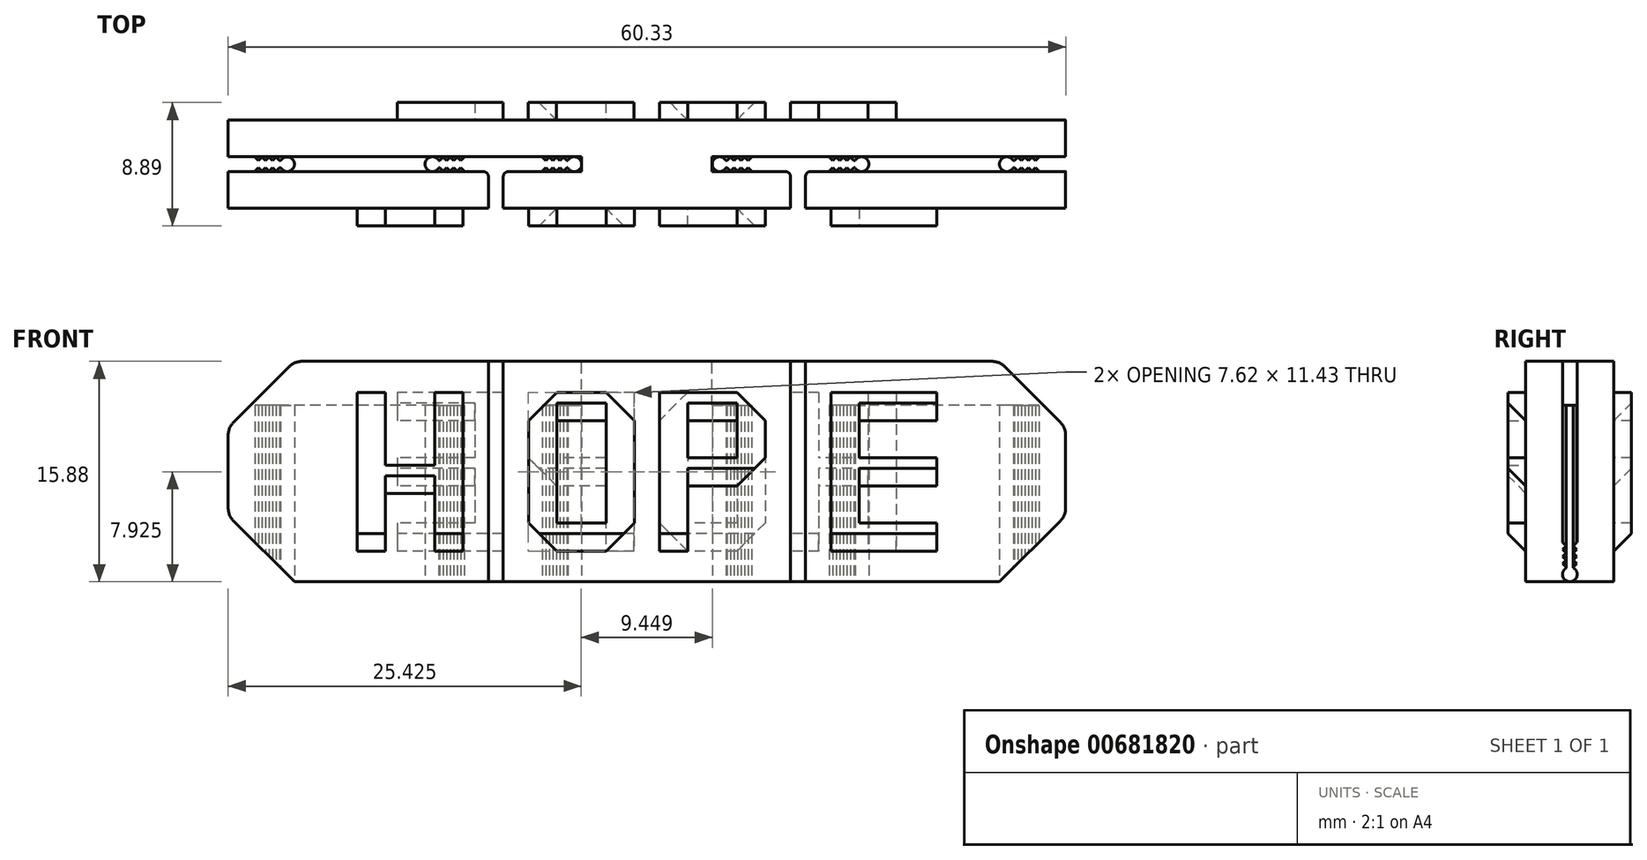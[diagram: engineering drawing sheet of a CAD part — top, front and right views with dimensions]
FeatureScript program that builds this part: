
annotation { "Feature Type Name" : "Feature", "Feature Type Description" : "" }
export const myFeature = defineFeature(function(context is Context, id is Id, definition is map)
    precondition{}
    {
        {
            var Q0;
            Q0=qCreatedBy(makeId("Front.planeOp"),FACE);
            var sketch = newSketch(context, id + "F0", { "sketchPlane" : qUnion([Q0])});
            skLineSegment(sketch, "E0.bottom", {"start": v(0, 0) * mm, "end": v(60.33, 0) * mm});
            skLineSegment(sketch, "E0.top", {"start": v(0, 15.88) * mm, "end": v(60.33, 15.88) * mm});
            skLineSegment(sketch, "E0.left", {"start": v(0, 0) * mm, "end": v(0, 15.88) * mm});
            skLineSegment(sketch, "E0.right", {"start": v(60.33, 0) * mm, "end": v(60.33, 15.88) * mm});
            skSolve(sketch);
        }
        {
            var Q0;
            Q0=makeQuery(id+"F0.imprint","IMPRINT",FACE,{"disambiguationData":[TD([[makeQuery(id+"F0.imprint","IMPRINT",EDGE,{"derivedFrom":sQuery(id+"F0.wireOp",EDGE,"E0.bottom")}),1.0]])]});
            extrude(context, id + "F1", {"entities" : qUnion([Q0]), "depth" : 6.35 * mm, "offsetDistance" : 25.4 * mm});
        }
        {
            var Q0;
            Q0=makeQuery(id+"F1.opExtrude","SWEPT_FACE",FACE,{"disambiguationData":[OSD([sQuery(id+"F0.wireOp",EDGE,"E0.top")])]});
            var sketch = newSketch(context, id + "F2", { "sketchPlane" : qUnion([Q0])});
            skLineSegment(sketch, "E1", {"start": v(0, -2.64) * mm, "end": v(60.33, -2.64) * mm});
            skLineSegment(sketch, "E2", {"start": v(0, -3.7) * mm, "end": v(18.75, -3.7) * mm});
            skLineSegment(sketch, "E3", {"start": v(4.78, -2.64) * mm, "end": v(4.78, -3.7) * mm});
            skLineSegment(sketch, "E4", {"start": v(14.17, -2.64) * mm, "end": v(14.17, -3.7) * mm});
            skLineSegment(sketch, "E5", {"start": v(25.46, -2.64) * mm, "end": v(25.46, -3.7) * mm});
            skLineSegment(sketch, "E6", {"start": v(34.86, -2.64) * mm, "end": v(34.86, -3.7) * mm});
            skLineSegment(sketch, "E7", {"start": v(55.55, -3.7) * mm, "end": v(55.55, -2.64) * mm});
            skLineSegment(sketch, "E8", {"start": v(46.15, -3.7) * mm, "end": v(46.15, -2.64) * mm});
            skLineSegment(sketch, "E9", {"start": v(41.58, -3.7) * mm, "end": v(41.58, -6.35) * mm});
            skLineSegment(sketch, "E10", {"start": v(40.51, -6.35) * mm, "end": v(40.51, -3.7) * mm});
            skLineSegment(sketch, "E11", {"start": v(18.75, -6.35) * mm, "end": v(18.75, -3.7) * mm});
            skLineSegment(sketch, "E12", {"start": v(19.81, -6.35) * mm, "end": v(19.81, -3.7) * mm});
            skLineSegment(sketch, "E13.trimOffspring", {"start": v(41.58, -3.7) * mm, "end": v(60.33, -3.7) * mm});
            skLineSegment(sketch, "E14.trimOffspring", {"start": v(19.81, -3.7) * mm, "end": v(40.51, -3.7) * mm});
            skSolve(sketch);
        }
        {
            var Q0;
            {var subQ3=sQuery(id+"F2.wireOp",EDGE,"E7");Q0=makeQuery(id+"F2.imprint","IMPRINT",FACE,{"disambiguationData":[TD([[makeQuery(id+"F2.imprint","IMPRINT",EDGE,{"derivedFrom":subQ3}),-1.0]])]});}
            var Q1;
            {var subQ2=sQuery(id+"F2.wireOp",EDGE,"E6");Q1=makeQuery(id+"F2.imprint","IMPRINT",FACE,{"disambiguationData":[TD([[makeQuery(id+"F2.imprint","IMPRINT",EDGE,{"derivedFrom":subQ2}),1.0]])]});}
            var Q2;
            {var subQ0=sQuery(id+"F2.wireOp",EDGE,"E4");Q2=makeQuery(id+"F2.imprint","IMPRINT",FACE,{"disambiguationData":[TD([[makeQuery(id+"F2.imprint","IMPRINT",EDGE,{"derivedFrom":subQ0}),1.0]])]});}
            var Q3;
            {var subQ3=sQuery(id+"F2.wireOp",EDGE,"E3");Q3=makeQuery(id+"F2.imprint","IMPRINT",FACE,{"disambiguationData":[TD([[makeQuery(id+"F2.imprint","IMPRINT",EDGE,{"derivedFrom":subQ3}),-1.0]])]});}
            extrude(context, id + "F3", {"entities" : qUnion([Q0, Q1, Q2, Q3]), "operationType" : NewBodyOperationType.REMOVE, "oppositeDirection" : true, "depth" : 25.4 * mm, "offsetDistance" : 25.4 * mm});
        }
        {
            var Q0;
            {var subQ0=sQuery(id+"F0.wireOp",EDGE,"E0.left");var subQ1=sQuery(id+"F0.wireOp",EDGE,"E0.top");var subQ2=sQuery(id+"F2.wireOp",EDGE,"E1");var subQ3=makeQuery(id+"F1.opExtrude","SWEPT_EDGE",EDGE,{"disambiguationData":[OSD([subQ1,subQ0])]});Q0=makeQuery(id+"F3.boolean.opBoolean","SPLIT",EDGE,{"disambiguationData":[TD([makeQuery(id+"F3.opExtrude","SWEPT_FACE",FACE,{"disambiguationData":[OSD([subQ2]),TDD([makeQuery(id+"F2.imprint","IMPRINT",EDGE,{"disambiguationData":[TD([[makeQuery(id+"F2.imprint","INTERSECT",VERTEX,{"derivedFrom":[subQ2,sQuery(id+"F2.wireOp",EDGE,"E3")]}),1.0]])],"derivedFrom":subQ2})])]})])],"derivedFrom":subQ3});}
            var Q1;
            {var subQ0=sQuery(id+"F0.wireOp",EDGE,"E0.left");var subQ1=sQuery(id+"F0.wireOp",EDGE,"E0.top");var subQ2=sQuery(id+"F2.wireOp",EDGE,"E2");var subQ3=makeQuery(id+"F1.opExtrude","SWEPT_EDGE",EDGE,{"disambiguationData":[OSD([subQ1,subQ0])]});Q1=makeQuery(id+"F3.boolean.opBoolean","SPLIT",EDGE,{"disambiguationData":[TD([makeQuery(id+"F3.opExtrude","SWEPT_FACE",FACE,{"disambiguationData":[OSD([subQ2]),TDD([makeQuery(id+"F2.imprint","IMPRINT",EDGE,{"disambiguationData":[TD([[makeQuery(id+"F2.imprint","INTERSECT",VERTEX,{"derivedFrom":[subQ2,sQuery(id+"F2.wireOp",EDGE,"E3")]}),1.0]])],"derivedFrom":subQ2})])]})])],"derivedFrom":subQ3});}
            var Q2;
            {var subQ0=sQuery(id+"F0.wireOp",EDGE,"E0.bottom");var subQ1=sQuery(id+"F2.wireOp",EDGE,"E1");var subQ2=sQuery(id+"F0.wireOp",EDGE,"E0.left");Q2=makeQuery(id+"F3.boolean.opBoolean","SPLIT",EDGE,{"disambiguationData":[TD([makeQuery(id+"F3.opExtrude","SWEPT_FACE",FACE,{"disambiguationData":[OSD([subQ1]),TDD([makeQuery(id+"F2.imprint","IMPRINT",EDGE,{"disambiguationData":[TD([[makeQuery(id+"F2.imprint","INTERSECT",VERTEX,{"derivedFrom":[subQ1,sQuery(id+"F2.wireOp",EDGE,"E3")]}),1.0]])],"derivedFrom":subQ1})])]})])],"derivedFrom":makeQuery(id+"F1.opExtrude","SWEPT_EDGE",EDGE,{"disambiguationData":[OSD([subQ0,subQ2])]})});}
            var Q3;
            {var subQ0=sQuery(id+"F0.wireOp",EDGE,"E0.bottom");var subQ1=sQuery(id+"F0.wireOp",EDGE,"E0.left");var subQ3=sQuery(id+"F2.wireOp",EDGE,"E2");Q3=makeQuery(id+"F3.boolean.opBoolean","SPLIT",EDGE,{"disambiguationData":[TD([makeQuery(id+"F3.opExtrude","SWEPT_FACE",FACE,{"disambiguationData":[OSD([subQ3]),TDD([makeQuery(id+"F2.imprint","IMPRINT",EDGE,{"disambiguationData":[TD([[makeQuery(id+"F2.imprint","INTERSECT",VERTEX,{"derivedFrom":[subQ3,sQuery(id+"F2.wireOp",EDGE,"E3")]}),1.0]])],"derivedFrom":subQ3})])]})])],"derivedFrom":makeQuery(id+"F1.opExtrude","SWEPT_EDGE",EDGE,{"disambiguationData":[OSD([subQ0,subQ1])]})});}
            var Q4;
            {var subQ0=sQuery(id+"F0.wireOp",EDGE,"E0.bottom");var subQ1=sQuery(id+"F0.wireOp",EDGE,"E0.right");var subQ3=sQuery(id+"F2.wireOp",EDGE,"E1");Q4=makeQuery(id+"F3.boolean.opBoolean","SPLIT",EDGE,{"disambiguationData":[TD([makeQuery(id+"F3.opExtrude","SWEPT_FACE",FACE,{"disambiguationData":[OSD([subQ3]),TDD([makeQuery(id+"F2.imprint","IMPRINT",EDGE,{"disambiguationData":[TD([[makeQuery(id+"F2.imprint","INTERSECT",VERTEX,{"derivedFrom":[subQ3,sQuery(id+"F2.wireOp",EDGE,"E7")]}),-1.0]])],"derivedFrom":subQ3})])]})])],"derivedFrom":makeQuery(id+"F1.opExtrude","SWEPT_EDGE",EDGE,{"disambiguationData":[OSD([subQ0,subQ1])]})});}
            var Q5;
            {var subQ0=sQuery(id+"F0.wireOp",EDGE,"E0.bottom");var subQ1=sQuery(id+"F0.wireOp",EDGE,"E0.right");var subQ2=sQuery(id+"F2.wireOp",EDGE,"E13.trimOffspring");Q5=makeQuery(id+"F3.boolean.opBoolean","SPLIT",EDGE,{"disambiguationData":[TD([makeQuery(id+"F3.opExtrude","SWEPT_FACE",FACE,{"disambiguationData":[OSD([subQ2]),TDD([makeQuery(id+"F2.imprint","IMPRINT",EDGE,{"disambiguationData":[TD([[makeQuery(id+"F2.imprint","INTERSECT",VERTEX,{"derivedFrom":[sQuery(id+"F2.wireOp",EDGE,"E7"),subQ2]}),-1.0]])],"derivedFrom":subQ2})])]})])],"derivedFrom":makeQuery(id+"F1.opExtrude","SWEPT_EDGE",EDGE,{"disambiguationData":[OSD([subQ0,subQ1])]})});}
            var Q6;
            {var subQ0=sQuery(id+"F0.wireOp",EDGE,"E0.right");var subQ1=sQuery(id+"F0.wireOp",EDGE,"E0.top");var subQ2=sQuery(id+"F2.wireOp",EDGE,"E13.trimOffspring");var subQ3=makeQuery(id+"F1.opExtrude","SWEPT_EDGE",EDGE,{"disambiguationData":[OSD([subQ1,subQ0])]});Q6=makeQuery(id+"F3.boolean.opBoolean","SPLIT",EDGE,{"disambiguationData":[TD([makeQuery(id+"F3.opExtrude","SWEPT_FACE",FACE,{"disambiguationData":[OSD([subQ2]),TDD([makeQuery(id+"F2.imprint","IMPRINT",EDGE,{"disambiguationData":[TD([[makeQuery(id+"F2.imprint","INTERSECT",VERTEX,{"derivedFrom":[sQuery(id+"F2.wireOp",EDGE,"E7"),subQ2]}),-1.0]])],"derivedFrom":subQ2})])]})])],"derivedFrom":subQ3});}
            var Q7;
            {var subQ0=sQuery(id+"F0.wireOp",EDGE,"E0.right");var subQ1=sQuery(id+"F0.wireOp",EDGE,"E0.top");var subQ2=sQuery(id+"F2.wireOp",EDGE,"E1");var subQ3=makeQuery(id+"F1.opExtrude","SWEPT_EDGE",EDGE,{"disambiguationData":[OSD([subQ1,subQ0])]});Q7=makeQuery(id+"F3.boolean.opBoolean","SPLIT",EDGE,{"disambiguationData":[TD([makeQuery(id+"F3.opExtrude","SWEPT_FACE",FACE,{"disambiguationData":[OSD([subQ2]),TDD([makeQuery(id+"F2.imprint","IMPRINT",EDGE,{"disambiguationData":[TD([[makeQuery(id+"F2.imprint","INTERSECT",VERTEX,{"derivedFrom":[subQ2,sQuery(id+"F2.wireOp",EDGE,"E7")]}),-1.0]])],"derivedFrom":subQ2})])]})])],"derivedFrom":subQ3});}
            chamfer(context, id + "F4", {"entities" : qUnion([Q0, Q1, Q2, Q3, Q4, Q5, Q6, Q7]), "width" : 4.78 * mm, "tangentPropagation" : true});
        }
        {
            var Q0;
            {var subQ0=sQuery(id+"F0.wireOp",EDGE,"E0.bottom");var subQ1=sQuery(id+"F0.wireOp",EDGE,"E0.top");Q0=makeQuery(id+"F3.boolean.opBoolean","SPLIT",FACE,{"disambiguationData":[TD([makeQuery(id+"F3.opExtrude","SWEPT_FACE",FACE,{"disambiguationData":[OSD([sQuery(id+"F2.wireOp",EDGE,"E10")])]})])],"derivedFrom":makeQuery(id+"F1.opExtrude","CAP_FACE",FACE,{"disambiguationData":[OSD([subQ0,subQ1,sQuery(id+"F0.wireOp",EDGE,"E0.left"),sQuery(id+"F0.wireOp",EDGE,"E0.right")])],"isStart":false})});}
            var sketch = newSketch(context, id + "F5", { "sketchPlane" : qUnion([Q0])});
            skLineSegment(sketch, "E15.bottom", {"start": v(23.67, 13.64) * mm, "end": v(27.23, 13.64) * mm});
            skLineSegment(sketch, "E15.top", {"start": v(23.67, 2.2) * mm, "end": v(25.2, 2.2) * mm});
            skLineSegment(sketch, "E15.left", {"start": v(21.64, 11.6) * mm, "end": v(21.64, 6.27) * mm});
            skLineSegment(sketch, "E15.right", {"start": v(29.26, 11.6) * mm, "end": v(29.26, 4.24) * mm});
            skLineSegment(sketch, "E16", {"start": v(21.64, 11.6) * mm, "end": v(23.67, 13.64) * mm});
            skLineSegment(sketch, "E17", {"start": v(27.23, 13.64) * mm, "end": v(29.26, 11.6) * mm});
            skLineSegment(sketch, "E18", {"start": v(21.64, 4.24) * mm, "end": v(23.67, 2.2) * mm});
            skLineSegment(sketch, "E19", {"start": v(27.23, 2.2) * mm, "end": v(29.26, 4.24) * mm});
            skLineSegment(sketch, "E20", {"start": v(21.64, 9.58) * mm, "end": v(25.7, 13.64) * mm});
            skLineSegment(sketch, "E21", {"start": v(25.2, 13.64) * mm, "end": v(29.26, 9.58) * mm});
            skLineSegment(sketch, "E22", {"start": v(21.64, 6.27) * mm, "end": v(25.7, 2.2) * mm});
            skLineSegment(sketch, "E23", {"start": v(25.2, 2.2) * mm, "end": v(29.26, 6.27) * mm});
            skLineSegment(sketch, "E24", {"start": v(21.64, 11.6) * mm, "end": v(29.26, 11.6) * mm});
            skLineSegment(sketch, "E25", {"start": v(23.67, 13.64) * mm, "end": v(23.67, 2.2) * mm});
            skLineSegment(sketch, "E26", {"start": v(21.64, 4.24) * mm, "end": v(29.26, 4.24) * mm});
            skLineSegment(sketch, "E27", {"start": v(27.23, 13.64) * mm, "end": v(27.23, 2.2) * mm});
            skPoint(sketch, "E28.orphan", {"position": v(21.64, 13.64) * mm});
            skPoint(sketch, "E29.orphan", {"position": v(29.26, 13.64) * mm});
            skPoint(sketch, "E30.orphan", {"position": v(29.26, 2.2) * mm});
            skPoint(sketch, "E31.orphan", {"position": v(21.64, 2.2) * mm});
            skLineSegment(sketch, "E32", {"start": v(21.64, 4.24) * mm, "end": v(21.64, 6.27) * mm});
            skLineSegment(sketch, "E33", {"start": v(25.2, 2.2) * mm, "end": v(27.23, 2.2) * mm});
            skLineSegment(sketch, "E34.bottom", {"start": v(31.06, 13.64) * mm, "end": v(36.65, 13.64) * mm});
            skLineSegment(sketch, "E34.top", {"start": v(31.06, 2.2) * mm, "end": v(33.1, 2.2) * mm});
            skLineSegment(sketch, "E34.left", {"start": v(31.06, 13.64) * mm, "end": v(31.06, 2.2) * mm});
            skLineSegment(sketch, "E34.right", {"start": v(38.68, 11.6) * mm, "end": v(38.68, 8.94) * mm});
            skLineSegment(sketch, "E35", {"start": v(33.1, 13.64) * mm, "end": v(33.1, 2.2) * mm});
            skLineSegment(sketch, "E36", {"start": v(31.06, 11.6) * mm, "end": v(38.68, 11.6) * mm});
            skLineSegment(sketch, "E37", {"start": v(36.65, 13.64) * mm, "end": v(38.68, 11.6) * mm});
            skLineSegment(sketch, "E38", {"start": v(31.06, 6.9) * mm, "end": v(36.65, 6.9) * mm});
            skLineSegment(sketch, "E39", {"start": v(31.06, 8.94) * mm, "end": v(38.68, 8.94) * mm});
            skLineSegment(sketch, "E40", {"start": v(36.65, 13.64) * mm, "end": v(36.65, 6.9) * mm});
            skLineSegment(sketch, "E41", {"start": v(36.65, 6.9) * mm, "end": v(38.68, 8.94) * mm});
            skSolve(sketch);
        }
        {
            var Q0;
            {var subQ0=sQuery(id+"F5.wireOp",EDGE,"E17");Q0=makeQuery(id+"F5.imprint","IMPRINT",FACE,{"disambiguationData":[TD([[makeQuery(id+"F5.imprint","IMPRINT",EDGE,{"derivedFrom":subQ0}),-1.0]])]});}
            var Q1;
            {var subQ1=sQuery(id+"F5.wireOp",EDGE,"E15.bottom");var subQ3=sQuery(id+"F5.wireOp",EDGE,"E20");var subQ4=makeQuery(id+"F5.imprint","INTERSECT",VERTEX,{"derivedFrom":[subQ1,subQ3]});Q1=makeQuery(id+"F5.imprint","IMPRINT",FACE,{"disambiguationData":[TD([[makeQuery(id+"F5.imprint","IMPRINT",EDGE,{"disambiguationData":[TD([[subQ4,1.0]])],"derivedFrom":subQ3}),-1.0]])]});}
            var Q2;
            {var subQ0=sQuery(id+"F5.wireOp",EDGE,"E20");var subQ1=sQuery(id+"F5.wireOp",EDGE,"E15.bottom");var subQ2=makeQuery(id+"F5.imprint","INTERSECT",VERTEX,{"derivedFrom":[subQ1,subQ0]});Q2=makeQuery(id+"F5.imprint","IMPRINT",FACE,{"disambiguationData":[TD([[makeQuery(id+"F5.imprint","IMPRINT",EDGE,{"disambiguationData":[TD([[subQ2,1.0]])],"derivedFrom":subQ1}),-1.0]])]});}
            var Q3;
            {var subQ1=sQuery(id+"F5.wireOp",EDGE,"E15.right");var subQ3=sQuery(id+"F5.wireOp",EDGE,"E21");var subQ4=makeQuery(id+"F5.imprint","INTERSECT",VERTEX,{"derivedFrom":[subQ1,subQ3]});Q3=makeQuery(id+"F5.imprint","IMPRINT",FACE,{"disambiguationData":[TD([[makeQuery(id+"F5.imprint","IMPRINT",EDGE,{"disambiguationData":[TD([[subQ4,1.0]])],"derivedFrom":subQ1}),-1.0]])]});}
            var Q4;
            {var subQ0=sQuery(id+"F5.wireOp",EDGE,"E21");var subQ1=sQuery(id+"F5.wireOp",EDGE,"E15.right");var subQ2=makeQuery(id+"F5.imprint","INTERSECT",VERTEX,{"derivedFrom":[subQ1,subQ0]});Q4=makeQuery(id+"F5.imprint","IMPRINT",FACE,{"disambiguationData":[TD([[makeQuery(id+"F5.imprint","IMPRINT",EDGE,{"disambiguationData":[TD([[subQ2,-1.0]])],"derivedFrom":subQ1}),-1.0]])]});}
            var Q5;
            {var subQ1=sQuery(id+"F5.wireOp",EDGE,"E15.right");var subQ3=sQuery(id+"F5.wireOp",EDGE,"E23");var subQ4=makeQuery(id+"F5.imprint","INTERSECT",VERTEX,{"derivedFrom":[subQ1,subQ3]});Q5=makeQuery(id+"F5.imprint","IMPRINT",FACE,{"disambiguationData":[TD([[makeQuery(id+"F5.imprint","IMPRINT",EDGE,{"disambiguationData":[TD([[subQ4,-1.0]])],"derivedFrom":subQ1}),-1.0]])]});}
            var Q6;
            {var subQ0=sQuery(id+"F5.wireOp",EDGE,"E19");Q6=makeQuery(id+"F5.imprint","IMPRINT",FACE,{"disambiguationData":[TD([[makeQuery(id+"F5.imprint","IMPRINT",EDGE,{"derivedFrom":subQ0}),1.0]])]});}
            var Q7;
            {var subQ0=sQuery(id+"F5.wireOp",EDGE,"E33");var subQ1=sQuery(id+"F5.wireOp",EDGE,"E22");var subQ2=makeQuery(id+"F5.imprint","INTERSECT",VERTEX,{"derivedFrom":[subQ1,subQ0]});Q7=makeQuery(id+"F5.imprint","IMPRINT",FACE,{"disambiguationData":[TD([[makeQuery(id+"F5.imprint","IMPRINT",EDGE,{"disambiguationData":[TD([[subQ2,1.0]])],"derivedFrom":subQ1}),1.0]])]});}
            var Q8;
            {var subQ0=sQuery(id+"F5.wireOp",EDGE,"E33");var subQ1=sQuery(id+"F5.wireOp",EDGE,"E22");var subQ2=makeQuery(id+"F5.imprint","INTERSECT",VERTEX,{"derivedFrom":[subQ1,subQ0]});Q8=makeQuery(id+"F5.imprint","IMPRINT",FACE,{"disambiguationData":[TD([[makeQuery(id+"F5.imprint","IMPRINT",EDGE,{"disambiguationData":[TD([[subQ2,1.0]])],"derivedFrom":subQ1}),-1.0]])]});}
            var Q9;
            {var subQ0=sQuery(id+"F5.wireOp",EDGE,"E23");var subQ1=sQuery(id+"F5.wireOp",EDGE,"E22");var subQ2=makeQuery(id+"F5.imprint","INTERSECT",VERTEX,{"derivedFrom":[subQ1,subQ0]});Q9=makeQuery(id+"F5.imprint","IMPRINT",FACE,{"disambiguationData":[TD([[makeQuery(id+"F5.imprint","IMPRINT",EDGE,{"disambiguationData":[TD([[subQ2,1.0]])],"derivedFrom":subQ1}),1.0]])]});}
            var Q10;
            {var subQ0=sQuery(id+"F5.wireOp",EDGE,"E15.top");Q10=makeQuery(id+"F5.imprint","IMPRINT",FACE,{"disambiguationData":[TD([[makeQuery(id+"F5.imprint","IMPRINT",EDGE,{"derivedFrom":subQ0}),1.0]])]});}
            var Q11;
            {var subQ0=sQuery(id+"F5.wireOp",EDGE,"E18");Q11=makeQuery(id+"F5.imprint","IMPRINT",FACE,{"disambiguationData":[TD([[makeQuery(id+"F5.imprint","IMPRINT",EDGE,{"derivedFrom":subQ0}),1.0]])]});}
            var Q12;
            {var subQ0=sQuery(id+"F5.wireOp",EDGE,"E32");Q12=makeQuery(id+"F5.imprint","IMPRINT",FACE,{"disambiguationData":[TD([[makeQuery(id+"F5.imprint","IMPRINT",EDGE,{"derivedFrom":subQ0}),-1.0]])]});}
            var Q13;
            {var subQ1=sQuery(id+"F5.wireOp",EDGE,"E15.left");var subQ3=sQuery(id+"F5.wireOp",EDGE,"E20");var subQ4=makeQuery(id+"F5.imprint","INTERSECT",VERTEX,{"derivedFrom":[subQ1,subQ3]});Q13=makeQuery(id+"F5.imprint","IMPRINT",FACE,{"disambiguationData":[TD([[makeQuery(id+"F5.imprint","IMPRINT",EDGE,{"disambiguationData":[TD([[subQ4,-1.0]])],"derivedFrom":subQ1}),1.0]])]});}
            var Q14;
            {var subQ0=sQuery(id+"F5.wireOp",EDGE,"E21");var subQ1=sQuery(id+"F5.wireOp",EDGE,"E20");var subQ2=makeQuery(id+"F5.imprint","INTERSECT",VERTEX,{"derivedFrom":[subQ1,subQ0]});Q14=makeQuery(id+"F5.imprint","IMPRINT",FACE,{"disambiguationData":[TD([[makeQuery(id+"F5.imprint","IMPRINT",EDGE,{"disambiguationData":[TD([[subQ2,1.0]])],"derivedFrom":subQ1}),-1.0]])]});}
            var Q15;
            {var subQ1=sQuery(id+"F5.wireOp",EDGE,"E15.bottom");var subQ3=sQuery(id+"F5.wireOp",EDGE,"E21");var subQ4=makeQuery(id+"F5.imprint","INTERSECT",VERTEX,{"derivedFrom":[subQ1,subQ3]});Q15=makeQuery(id+"F5.imprint","IMPRINT",FACE,{"disambiguationData":[TD([[makeQuery(id+"F5.imprint","IMPRINT",EDGE,{"disambiguationData":[TD([[subQ4,-1.0]])],"derivedFrom":subQ3}),-1.0]])]});}
            var Q16;
            {var subQ0=sQuery(id+"F5.wireOp",EDGE,"E16");Q16=makeQuery(id+"F5.imprint","IMPRINT",FACE,{"disambiguationData":[TD([[makeQuery(id+"F5.imprint","IMPRINT",EDGE,{"derivedFrom":subQ0}),-1.0]])]});}
            var Q17;
            {var subQ1=sQuery(id+"F5.wireOp",EDGE,"E15.left");var subQ3=sQuery(id+"F5.wireOp",EDGE,"E20");var subQ4=makeQuery(id+"F5.imprint","INTERSECT",VERTEX,{"derivedFrom":[subQ1,subQ3]});Q17=makeQuery(id+"F5.imprint","IMPRINT",FACE,{"disambiguationData":[TD([[makeQuery(id+"F5.imprint","IMPRINT",EDGE,{"disambiguationData":[TD([[subQ4,1.0]])],"derivedFrom":subQ1}),1.0]])]});}
            var Q18;
            {var subQ0=sQuery(id+"F5.wireOp",EDGE,"E34.top");Q18=makeQuery(id+"F5.imprint","IMPRINT",FACE,{"disambiguationData":[TD([[makeQuery(id+"F5.imprint","IMPRINT",EDGE,{"derivedFrom":subQ0}),1.0]])]});}
            var Q19;
            {var subQ0=sQuery(id+"F5.wireOp",EDGE,"E38");var subQ1=sQuery(id+"F5.wireOp",EDGE,"E34.left");var subQ2=makeQuery(id+"F5.imprint","INTERSECT",VERTEX,{"derivedFrom":[subQ1,subQ0]});Q19=makeQuery(id+"F5.imprint","IMPRINT",FACE,{"disambiguationData":[TD([[makeQuery(id+"F5.imprint","IMPRINT",EDGE,{"disambiguationData":[TD([[subQ2,1.0]])],"derivedFrom":subQ1}),1.0]])]});}
            var Q20;
            {var subQ0=sQuery(id+"F5.wireOp",EDGE,"E36");var subQ1=sQuery(id+"F5.wireOp",EDGE,"E34.left");var subQ2=makeQuery(id+"F5.imprint","INTERSECT",VERTEX,{"derivedFrom":[subQ1,subQ0]});Q20=makeQuery(id+"F5.imprint","IMPRINT",FACE,{"disambiguationData":[TD([[makeQuery(id+"F5.imprint","IMPRINT",EDGE,{"disambiguationData":[TD([[subQ2,-1.0]])],"derivedFrom":subQ1}),1.0]])]});}
            var Q21;
            {var subQ0=sQuery(id+"F5.wireOp",EDGE,"E34.left");var subQ1=sQuery(id+"F5.wireOp",EDGE,"E34.bottom");var subQ2=makeQuery(id+"F5.imprint","INTERSECT",VERTEX,{"derivedFrom":[subQ1,subQ0]});Q21=makeQuery(id+"F5.imprint","IMPRINT",FACE,{"disambiguationData":[TD([[makeQuery(id+"F5.imprint","IMPRINT",EDGE,{"disambiguationData":[TD([[subQ2,-1.0]])],"derivedFrom":subQ1}),-1.0]])]});}
            var Q22;
            {var subQ1=sQuery(id+"F5.wireOp",EDGE,"E34.bottom");var subQ3=sQuery(id+"F5.wireOp",EDGE,"E35");var subQ4=makeQuery(id+"F5.imprint","INTERSECT",VERTEX,{"derivedFrom":[subQ1,subQ3]});Q22=makeQuery(id+"F5.imprint","IMPRINT",FACE,{"disambiguationData":[TD([[makeQuery(id+"F5.imprint","IMPRINT",EDGE,{"disambiguationData":[TD([[subQ4,-1.0]])],"derivedFrom":subQ3}),1.0]])]});}
            var Q23;
            {var subQ0=sQuery(id+"F5.wireOp",EDGE,"E39");var subQ1=sQuery(id+"F5.wireOp",EDGE,"E35");var subQ2=makeQuery(id+"F5.imprint","INTERSECT",VERTEX,{"derivedFrom":[subQ1,subQ0]});Q23=makeQuery(id+"F5.imprint","IMPRINT",FACE,{"disambiguationData":[TD([[makeQuery(id+"F5.imprint","IMPRINT",EDGE,{"disambiguationData":[TD([[subQ2,-1.0]])],"derivedFrom":subQ1}),1.0]])]});}
            var Q24;
            {var subQ0=sQuery(id+"F5.wireOp",EDGE,"E41");Q24=makeQuery(id+"F5.imprint","IMPRINT",FACE,{"disambiguationData":[TD([[makeQuery(id+"F5.imprint","IMPRINT",EDGE,{"derivedFrom":subQ0}),1.0]])]});}
            var Q25;
            {var subQ0=sQuery(id+"F5.wireOp",EDGE,"E37");Q25=makeQuery(id+"F5.imprint","IMPRINT",FACE,{"disambiguationData":[TD([[makeQuery(id+"F5.imprint","IMPRINT",EDGE,{"derivedFrom":subQ0}),-1.0]])]});}
            var Q26;
            {var subQ0=sQuery(id+"F5.wireOp",EDGE,"E34.right");Q26=makeQuery(id+"F5.imprint","IMPRINT",FACE,{"disambiguationData":[TD([[makeQuery(id+"F5.imprint","IMPRINT",EDGE,{"derivedFrom":subQ0}),-1.0]])]});}
            extrude(context, id + "F6", {"entities" : qUnion([Q0, Q1, Q2, Q3, Q4, Q5, Q6, Q7, Q8, Q9, Q10, Q11, Q12, Q13, Q14, Q15, Q16, Q17, Q18, Q19, Q20, Q21, Q22, Q23, Q24, Q25, Q26]), "operationType" : NewBodyOperationType.ADD, "depth" : 1.27 * mm, "offsetDistance" : 25.4 * mm});
        }
        {
            var Q0;
            {var subQ0=sQuery(id+"F0.wireOp",EDGE,"E0.bottom");var subQ1=sQuery(id+"F0.wireOp",EDGE,"E0.top");var subQ2=sQuery(id+"F0.wireOp",EDGE,"E0.left");Q0=makeQuery(id+"F3.boolean.opBoolean","SPLIT",FACE,{"disambiguationData":[TD([makeQuery(id+"F1.opExtrude","SWEPT_FACE",FACE,{"disambiguationData":[OSD([subQ2])]})])],"derivedFrom":makeQuery(id+"F1.opExtrude","CAP_FACE",FACE,{"disambiguationData":[OSD([subQ0,subQ1,subQ2,sQuery(id+"F0.wireOp",EDGE,"E0.right")])],"isStart":false})});}
            var sketch = newSketch(context, id + "F7", { "sketchPlane" : qUnion([Q0])});
            skLineSegment(sketch, "E42.bottom", {"start": v(9.3, 13.64) * mm, "end": v(11.33, 13.64) * mm});
            skLineSegment(sketch, "E42.top", {"start": v(9.3, 2.2) * mm, "end": v(11.33, 2.2) * mm});
            skLineSegment(sketch, "E42.left", {"start": v(9.3, 13.64) * mm, "end": v(9.3, 2.2) * mm});
            skLineSegment(sketch, "E42.right", {"start": v(16.92, 13.64) * mm, "end": v(16.92, 2.2) * mm});
            skLineSegment(sketch, "E43", {"start": v(11.33, 13.64) * mm, "end": v(11.33, 2.2) * mm});
            skLineSegment(sketch, "E44", {"start": v(14.88, 13.64) * mm, "end": v(14.88, 2.2) * mm});
            skLineSegment(sketch, "E45", {"start": v(9.3, 8.4) * mm, "end": v(16.92, 8.4) * mm});
            skLineSegment(sketch, "E46", {"start": v(9.3, 6.36) * mm, "end": v(16.92, 6.36) * mm});
            skLineSegment(sketch, "E47.trimOffspring", {"start": v(14.88, 13.64) * mm, "end": v(16.92, 13.64) * mm});
            skLineSegment(sketch, "E48.trimOffspring", {"start": v(14.88, 2.2) * mm, "end": v(16.92, 2.2) * mm});
            skSolve(sketch);
        }
        {
            var Q0;
            {var subQ0=sQuery(id+"F7.wireOp",EDGE,"E47.trimOffspring");Q0=makeQuery(id+"F7.imprint","IMPRINT",FACE,{"disambiguationData":[TD([[makeQuery(id+"F7.imprint","IMPRINT",EDGE,{"derivedFrom":subQ0}),-1.0]])]});}
            var Q1;
            {var subQ0=sQuery(id+"F7.wireOp",EDGE,"E45");var subQ1=sQuery(id+"F7.wireOp",EDGE,"E42.right");var subQ2=makeQuery(id+"F7.imprint","INTERSECT",VERTEX,{"derivedFrom":[subQ1,subQ0]});Q1=makeQuery(id+"F7.imprint","IMPRINT",FACE,{"disambiguationData":[TD([[makeQuery(id+"F7.imprint","IMPRINT",EDGE,{"disambiguationData":[TD([[subQ2,-1.0]])],"derivedFrom":subQ1}),-1.0]])]});}
            var Q2;
            {var subQ0=sQuery(id+"F7.wireOp",EDGE,"E48.trimOffspring");Q2=makeQuery(id+"F7.imprint","IMPRINT",FACE,{"disambiguationData":[TD([[makeQuery(id+"F7.imprint","IMPRINT",EDGE,{"derivedFrom":subQ0}),1.0]])]});}
            var Q3;
            {var subQ0=sQuery(id+"F7.wireOp",EDGE,"E45");var subQ1=sQuery(id+"F7.wireOp",EDGE,"E43");var subQ2=makeQuery(id+"F7.imprint","INTERSECT",VERTEX,{"derivedFrom":[subQ1,subQ0]});Q3=makeQuery(id+"F7.imprint","IMPRINT",FACE,{"disambiguationData":[TD([[makeQuery(id+"F7.imprint","IMPRINT",EDGE,{"disambiguationData":[TD([[subQ2,-1.0]])],"derivedFrom":subQ1}),1.0]])]});}
            var Q4;
            {var subQ0=sQuery(id+"F7.wireOp",EDGE,"E42.bottom");Q4=makeQuery(id+"F7.imprint","IMPRINT",FACE,{"disambiguationData":[TD([[makeQuery(id+"F7.imprint","IMPRINT",EDGE,{"derivedFrom":subQ0}),-1.0]])]});}
            var Q5;
            {var subQ0=sQuery(id+"F7.wireOp",EDGE,"E45");var subQ1=sQuery(id+"F7.wireOp",EDGE,"E42.left");var subQ2=makeQuery(id+"F7.imprint","INTERSECT",VERTEX,{"derivedFrom":[subQ1,subQ0]});Q5=makeQuery(id+"F7.imprint","IMPRINT",FACE,{"disambiguationData":[TD([[makeQuery(id+"F7.imprint","IMPRINT",EDGE,{"disambiguationData":[TD([[subQ2,-1.0]])],"derivedFrom":subQ1}),1.0]])]});}
            var Q6;
            {var subQ0=sQuery(id+"F7.wireOp",EDGE,"E42.top");Q6=makeQuery(id+"F7.imprint","IMPRINT",FACE,{"disambiguationData":[TD([[makeQuery(id+"F7.imprint","IMPRINT",EDGE,{"derivedFrom":subQ0}),1.0]])]});}
            extrude(context, id + "F8", {"entities" : qUnion([Q0, Q1, Q2, Q3, Q4, Q5, Q6]), "operationType" : NewBodyOperationType.ADD, "depth" : 1.27 * mm, "offsetDistance" : 25.4 * mm});
        }
        {
            var Q0;
            {var subQ0=sQuery(id+"F0.wireOp",EDGE,"E0.bottom");var subQ1=sQuery(id+"F0.wireOp",EDGE,"E0.right");var subQ2=sQuery(id+"F0.wireOp",EDGE,"E0.top");Q0=makeQuery(id+"F3.boolean.opBoolean","SPLIT",FACE,{"disambiguationData":[TD([makeQuery(id+"F1.opExtrude","SWEPT_FACE",FACE,{"disambiguationData":[OSD([subQ1])]})])],"derivedFrom":makeQuery(id+"F1.opExtrude","CAP_FACE",FACE,{"disambiguationData":[OSD([subQ0,subQ2,sQuery(id+"F0.wireOp",EDGE,"E0.left"),subQ1])],"isStart":false})});}
            var sketch = newSketch(context, id + "F9", { "sketchPlane" : qUnion([Q0])});
            skLineSegment(sketch, "E49.bottom", {"start": v(43.4, 13.64) * mm, "end": v(51.03, 13.64) * mm});
            skLineSegment(sketch, "E49.top", {"start": v(43.4, 2.2) * mm, "end": v(51.03, 2.2) * mm});
            skLineSegment(sketch, "E49.left", {"start": v(43.4, 13.64) * mm, "end": v(43.4, 2.2) * mm});
            skLineSegment(sketch, "E49.right", {"start": v(51.03, 13.64) * mm, "end": v(51.03, 11.6) * mm});
            skLineSegment(sketch, "E50", {"start": v(45.44, 13.64) * mm, "end": v(45.44, 2.2) * mm});
            skLineSegment(sketch, "E51", {"start": v(43.4, 11.6) * mm, "end": v(51.03, 11.6) * mm});
            skLineSegment(sketch, "E52", {"start": v(43.4, 4.24) * mm, "end": v(51.03, 4.24) * mm});
            skLineSegment(sketch, "E53", {"start": v(43.4, 8.94) * mm, "end": v(51.03, 8.94) * mm});
            skLineSegment(sketch, "E54", {"start": v(43.4, 6.9) * mm, "end": v(51.03, 6.9) * mm});
            skLineSegment(sketch, "E55.trimOffspring", {"start": v(51.03, 8.94) * mm, "end": v(51.03, 6.9) * mm});
            skLineSegment(sketch, "E56.trimOffspring", {"start": v(51.03, 4.24) * mm, "end": v(51.03, 2.2) * mm});
            skSolve(sketch);
        }
        {
            var Q0;
            {var subQ0=sQuery(id+"F9.wireOp",EDGE,"E49.left");var subQ1=sQuery(id+"F9.wireOp",EDGE,"E49.bottom");var subQ2=makeQuery(id+"F9.imprint","INTERSECT",VERTEX,{"derivedFrom":[subQ1,subQ0]});Q0=makeQuery(id+"F9.imprint","IMPRINT",FACE,{"disambiguationData":[TD([[makeQuery(id+"F9.imprint","IMPRINT",EDGE,{"disambiguationData":[TD([[subQ2,-1.0]])],"derivedFrom":subQ1}),-1.0]])]});}
            var Q1;
            {var subQ0=sQuery(id+"F9.wireOp",EDGE,"E49.right");Q1=makeQuery(id+"F9.imprint","IMPRINT",FACE,{"disambiguationData":[TD([[makeQuery(id+"F9.imprint","IMPRINT",EDGE,{"derivedFrom":subQ0}),-1.0]])]});}
            var Q2;
            {var subQ0=sQuery(id+"F9.wireOp",EDGE,"E51");var subQ1=sQuery(id+"F9.wireOp",EDGE,"E49.left");var subQ2=makeQuery(id+"F9.imprint","INTERSECT",VERTEX,{"derivedFrom":[subQ1,subQ0]});Q2=makeQuery(id+"F9.imprint","IMPRINT",FACE,{"disambiguationData":[TD([[makeQuery(id+"F9.imprint","IMPRINT",EDGE,{"disambiguationData":[TD([[subQ2,-1.0]])],"derivedFrom":subQ1}),1.0]])]});}
            var Q3;
            {var subQ0=sQuery(id+"F9.wireOp",EDGE,"E53");var subQ1=sQuery(id+"F9.wireOp",EDGE,"E49.left");var subQ2=makeQuery(id+"F9.imprint","INTERSECT",VERTEX,{"derivedFrom":[subQ1,subQ0]});Q3=makeQuery(id+"F9.imprint","IMPRINT",FACE,{"disambiguationData":[TD([[makeQuery(id+"F9.imprint","IMPRINT",EDGE,{"disambiguationData":[TD([[subQ2,-1.0]])],"derivedFrom":subQ1}),1.0]])]});}
            var Q4;
            {var subQ5=sQuery(id+"F9.wireOp",EDGE,"E55.trimOffspring");Q4=makeQuery(id+"F9.imprint","IMPRINT",FACE,{"disambiguationData":[TD([[makeQuery(id+"F9.imprint","IMPRINT",EDGE,{"derivedFrom":subQ5}),-1.0]])]});}
            var Q5;
            {var subQ0=sQuery(id+"F9.wireOp",EDGE,"E52");var subQ1=sQuery(id+"F9.wireOp",EDGE,"E49.left");var subQ2=makeQuery(id+"F9.imprint","INTERSECT",VERTEX,{"derivedFrom":[subQ1,subQ0]});Q5=makeQuery(id+"F9.imprint","IMPRINT",FACE,{"disambiguationData":[TD([[makeQuery(id+"F9.imprint","IMPRINT",EDGE,{"disambiguationData":[TD([[subQ2,1.0]])],"derivedFrom":subQ1}),1.0]])]});}
            var Q6;
            {var subQ0=sQuery(id+"F9.wireOp",EDGE,"E49.left");var subQ1=sQuery(id+"F9.wireOp",EDGE,"E49.top");var subQ2=makeQuery(id+"F9.imprint","INTERSECT",VERTEX,{"derivedFrom":[subQ1,subQ0]});Q6=makeQuery(id+"F9.imprint","IMPRINT",FACE,{"disambiguationData":[TD([[makeQuery(id+"F9.imprint","IMPRINT",EDGE,{"disambiguationData":[TD([[subQ2,-1.0]])],"derivedFrom":subQ1}),1.0]])]});}
            var Q7;
            {var subQ0=sQuery(id+"F9.wireOp",EDGE,"E56.trimOffspring");Q7=makeQuery(id+"F9.imprint","IMPRINT",FACE,{"disambiguationData":[TD([[makeQuery(id+"F9.imprint","IMPRINT",EDGE,{"derivedFrom":subQ0}),-1.0]])]});}
            extrude(context, id + "F10", {"entities" : qUnion([Q0, Q1, Q2, Q3, Q4, Q5, Q6, Q7]), "operationType" : NewBodyOperationType.ADD, "depth" : 1.27 * mm, "offsetDistance" : 25.4 * mm});
        }
        {
            var Q0;
            Q0=makeQuery(id+"F8.opExtrude","CAP_EDGE",EDGE,{"disambiguationData":[OSD([sQuery(id+"F7.wireOp",EDGE,"E42.top")])],"isStart":false});
            var Q1;
            Q1=makeQuery(id+"F8.opExtrude","CAP_EDGE",EDGE,{"disambiguationData":[OSD([sQuery(id+"F7.wireOp",EDGE,"E48.trimOffspring")])],"isStart":false});
            var Q2;
            Q2=makeQuery(id+"F6.opExtrude","CAP_EDGE",EDGE,{"disambiguationData":[OSD([sQuery(id+"F5.wireOp",EDGE,"E15.top"),sQuery(id+"F5.wireOp",EDGE,"E33")])],"isStart":false});
            var Q3;
            Q3=makeQuery(id+"F6.opExtrude","CAP_EDGE",EDGE,{"disambiguationData":[OSD([sQuery(id+"F5.wireOp",EDGE,"E34.top")])],"isStart":false});
            var Q4;
            Q4=makeQuery(id+"F10.opExtrude","CAP_EDGE",EDGE,{"disambiguationData":[OSD([sQuery(id+"F9.wireOp",EDGE,"E49.top")])],"isStart":false});
            var Q5;
            Q5=makeQuery(id+"F10.opExtrude","CAP_EDGE",EDGE,{"disambiguationData":[OSD([sQuery(id+"F9.wireOp",EDGE,"E54")])],"isStart":false});
            var Q6;
            Q6=makeQuery(id+"F10.opExtrude","CAP_EDGE",EDGE,{"disambiguationData":[OSD([sQuery(id+"F9.wireOp",EDGE,"E51")])],"isStart":false});
            var Q7;
            Q7=makeQuery(id+"F6.opExtrude","CAP_EDGE",EDGE,{"disambiguationData":[OSD([sQuery(id+"F5.wireOp",EDGE,"E36")])],"isStart":false});
            var Q8;
            Q8=makeQuery(id+"F6.opExtrude","CAP_EDGE",EDGE,{"disambiguationData":[OSD([sQuery(id+"F5.wireOp",EDGE,"E24")])],"isStart":false});
            var Q9;
            Q9=makeQuery(id+"F8.opExtrude","CAP_EDGE",EDGE,{"disambiguationData":[OSD([sQuery(id+"F7.wireOp",EDGE,"E46")])],"isStart":false});
            var Q10;
            Q10=makeQuery(id+"F6.opExtrude","CAP_EDGE",EDGE,{"disambiguationData":[OSD([sQuery(id+"F5.wireOp",EDGE,"E38")])],"isStart":false});
            chamfer(context, id + "F11", {"entities" : qUnion([Q0, Q1, Q2, Q3, Q4, Q5, Q6, Q7, Q8, Q9, Q10]), "width" : 1.27 * mm, "tangentPropagation" : true});
        }
        {
            var Q0;
            Q0=makeQuery(id+"F1.opExtrude","CAP_FACE",FACE,{"disambiguationData":[OSD([sQuery(id+"F0.wireOp",EDGE,"E0.bottom"),sQuery(id+"F0.wireOp",EDGE,"E0.top"),sQuery(id+"F0.wireOp",EDGE,"E0.left"),sQuery(id+"F0.wireOp",EDGE,"E0.right")])],"isStart":true});
            var sketch = newSketch(context, id + "F12", { "sketchPlane" : qUnion([Q0])});
            skLineSegment(sketch, "E57.bottom", {"start": v(-36.65, 13.64) * mm, "end": v(-33.1, 13.64) * mm});
            skLineSegment(sketch, "E57.top", {"start": v(-36.65, 2.2) * mm, "end": v(-35.13, 2.2) * mm});
            skLineSegment(sketch, "E57.left", {"start": v(-38.68, 11.6) * mm, "end": v(-38.68, 6.27) * mm});
            skLineSegment(sketch, "E57.right", {"start": v(-31.06, 11.6) * mm, "end": v(-31.06, 4.24) * mm});
            skLineSegment(sketch, "E58", {"start": v(-38.68, 11.6) * mm, "end": v(-36.65, 13.64) * mm});
            skLineSegment(sketch, "E59", {"start": v(-33.1, 13.64) * mm, "end": v(-31.06, 11.6) * mm});
            skLineSegment(sketch, "E60", {"start": v(-38.68, 4.24) * mm, "end": v(-36.65, 2.2) * mm});
            skLineSegment(sketch, "E61", {"start": v(-33.1, 2.2) * mm, "end": v(-31.06, 4.24) * mm});
            skLineSegment(sketch, "E62", {"start": v(-38.68, 9.58) * mm, "end": v(-34.62, 13.64) * mm});
            skLineSegment(sketch, "E63", {"start": v(-35.13, 13.64) * mm, "end": v(-31.06, 9.58) * mm});
            skLineSegment(sketch, "E64", {"start": v(-38.68, 6.27) * mm, "end": v(-34.62, 2.2) * mm});
            skLineSegment(sketch, "E65", {"start": v(-35.13, 2.2) * mm, "end": v(-31.06, 6.27) * mm});
            skLineSegment(sketch, "E66", {"start": v(-38.68, 11.6) * mm, "end": v(-31.06, 11.6) * mm});
            skLineSegment(sketch, "E67", {"start": v(-36.65, 13.64) * mm, "end": v(-36.65, 2.2) * mm});
            skLineSegment(sketch, "E68", {"start": v(-38.68, 4.24) * mm, "end": v(-31.06, 4.24) * mm});
            skLineSegment(sketch, "E69", {"start": v(-33.1, 13.64) * mm, "end": v(-33.1, 2.2) * mm});
            skPoint(sketch, "E70.orphan", {"position": v(-38.68, 13.64) * mm});
            skPoint(sketch, "E71.orphan", {"position": v(-31.06, 13.64) * mm});
            skPoint(sketch, "E72.orphan", {"position": v(-31.06, 2.2) * mm});
            skPoint(sketch, "E73.orphan", {"position": v(-38.68, 2.2) * mm});
            skLineSegment(sketch, "E74", {"start": v(-38.68, 4.24) * mm, "end": v(-38.68, 6.27) * mm});
            skLineSegment(sketch, "E75", {"start": v(-35.13, 2.2) * mm, "end": v(-33.1, 2.2) * mm});
            skLineSegment(sketch, "E76.bottom", {"start": v(-29.24, 13.64) * mm, "end": v(-23.65, 13.64) * mm});
            skLineSegment(sketch, "E76.top", {"start": v(-29.24, 2.2) * mm, "end": v(-27.2, 2.2) * mm});
            skLineSegment(sketch, "E76.left", {"start": v(-29.24, 13.64) * mm, "end": v(-29.24, 2.2) * mm});
            skLineSegment(sketch, "E76.right", {"start": v(-21.62, 11.6) * mm, "end": v(-21.62, 8.94) * mm});
            skLineSegment(sketch, "E77", {"start": v(-27.2, 13.64) * mm, "end": v(-27.2, 2.2) * mm});
            skLineSegment(sketch, "E78", {"start": v(-29.24, 11.6) * mm, "end": v(-21.62, 11.6) * mm});
            skLineSegment(sketch, "E79", {"start": v(-23.65, 13.64) * mm, "end": v(-21.62, 11.6) * mm});
            skLineSegment(sketch, "E80", {"start": v(-29.24, 6.9) * mm, "end": v(-23.65, 6.9) * mm});
            skLineSegment(sketch, "E81", {"start": v(-29.24, 8.94) * mm, "end": v(-21.62, 8.94) * mm});
            skLineSegment(sketch, "E82", {"start": v(-23.65, 13.64) * mm, "end": v(-23.65, 6.9) * mm});
            skLineSegment(sketch, "E83", {"start": v(-23.65, 6.9) * mm, "end": v(-21.62, 8.94) * mm});
            skLineSegment(sketch, "E84.bottom", {"start": v(-48.13, 13.64) * mm, "end": v(-46.1, 13.64) * mm});
            skLineSegment(sketch, "E84.top", {"start": v(-48.13, 2.2) * mm, "end": v(-46.1, 2.2) * mm});
            skLineSegment(sketch, "E84.left", {"start": v(-48.13, 13.64) * mm, "end": v(-48.13, 2.2) * mm});
            skLineSegment(sketch, "E84.right", {"start": v(-40.51, 13.64) * mm, "end": v(-40.51, 2.2) * mm});
            skLineSegment(sketch, "E85", {"start": v(-46.1, 13.64) * mm, "end": v(-46.1, 2.2) * mm});
            skLineSegment(sketch, "E86", {"start": v(-42.55, 13.64) * mm, "end": v(-42.55, 2.2) * mm});
            skLineSegment(sketch, "E87", {"start": v(-48.13, 8.94) * mm, "end": v(-40.51, 8.94) * mm});
            skLineSegment(sketch, "E88", {"start": v(-48.13, 6.9) * mm, "end": v(-40.51, 6.9) * mm});
            skLineSegment(sketch, "E89.trimOffspring", {"start": v(-42.55, 13.64) * mm, "end": v(-40.51, 13.64) * mm});
            skLineSegment(sketch, "E90.trimOffspring", {"start": v(-42.55, 2.2) * mm, "end": v(-40.51, 2.2) * mm});
            skLineSegment(sketch, "E91.bottom", {"start": v(-19.79, 13.64) * mm, "end": v(-12.17, 13.64) * mm});
            skLineSegment(sketch, "E91.top", {"start": v(-19.79, 2.2) * mm, "end": v(-12.17, 2.2) * mm});
            skLineSegment(sketch, "E91.left", {"start": v(-19.79, 13.64) * mm, "end": v(-19.79, 2.2) * mm});
            skLineSegment(sketch, "E91.right", {"start": v(-12.17, 13.64) * mm, "end": v(-12.17, 11.6) * mm});
            skLineSegment(sketch, "E92", {"start": v(-17.75, 13.64) * mm, "end": v(-17.75, 2.2) * mm});
            skLineSegment(sketch, "E93", {"start": v(-19.79, 11.6) * mm, "end": v(-12.17, 11.6) * mm});
            skLineSegment(sketch, "E94", {"start": v(-19.79, 4.24) * mm, "end": v(-12.17, 4.24) * mm});
            skLineSegment(sketch, "E95", {"start": v(-19.79, 8.94) * mm, "end": v(-12.17, 8.94) * mm});
            skLineSegment(sketch, "E96", {"start": v(-19.79, 6.9) * mm, "end": v(-12.17, 6.9) * mm});
            skLineSegment(sketch, "E97.trimOffspring", {"start": v(-12.17, 8.94) * mm, "end": v(-12.17, 6.9) * mm});
            skLineSegment(sketch, "E98.trimOffspring", {"start": v(-12.17, 4.24) * mm, "end": v(-12.17, 2.2) * mm});
            skSolve(sketch);
        }
        {
            var Q0;
            {var subQ0=sQuery(id+"F12.wireOp",EDGE,"E84.bottom");Q0=makeQuery(id+"F12.imprint","IMPRINT",FACE,{"disambiguationData":[TD([[makeQuery(id+"F12.imprint","IMPRINT",EDGE,{"derivedFrom":subQ0}),-1.0]])]});}
            var Q1;
            {var subQ0=sQuery(id+"F12.wireOp",EDGE,"E87");var subQ1=sQuery(id+"F12.wireOp",EDGE,"E84.left");var subQ2=makeQuery(id+"F12.imprint","INTERSECT",VERTEX,{"derivedFrom":[subQ1,subQ0]});Q1=makeQuery(id+"F12.imprint","IMPRINT",FACE,{"disambiguationData":[TD([[makeQuery(id+"F12.imprint","IMPRINT",EDGE,{"disambiguationData":[TD([[subQ2,-1.0]])],"derivedFrom":subQ1}),1.0]])]});}
            var Q2;
            {var subQ0=sQuery(id+"F12.wireOp",EDGE,"E84.top");Q2=makeQuery(id+"F12.imprint","IMPRINT",FACE,{"disambiguationData":[TD([[makeQuery(id+"F12.imprint","IMPRINT",EDGE,{"derivedFrom":subQ0}),1.0]])]});}
            var Q3;
            {var subQ0=sQuery(id+"F12.wireOp",EDGE,"E87");var subQ1=sQuery(id+"F12.wireOp",EDGE,"E85");var subQ2=makeQuery(id+"F12.imprint","INTERSECT",VERTEX,{"derivedFrom":[subQ1,subQ0]});Q3=makeQuery(id+"F12.imprint","IMPRINT",FACE,{"disambiguationData":[TD([[makeQuery(id+"F12.imprint","IMPRINT",EDGE,{"disambiguationData":[TD([[subQ2,-1.0]])],"derivedFrom":subQ1}),1.0]])]});}
            var Q4;
            {var subQ0=sQuery(id+"F12.wireOp",EDGE,"E89.trimOffspring");Q4=makeQuery(id+"F12.imprint","IMPRINT",FACE,{"disambiguationData":[TD([[makeQuery(id+"F12.imprint","IMPRINT",EDGE,{"derivedFrom":subQ0}),-1.0]])]});}
            var Q5;
            {var subQ0=sQuery(id+"F12.wireOp",EDGE,"E90.trimOffspring");Q5=makeQuery(id+"F12.imprint","IMPRINT",FACE,{"disambiguationData":[TD([[makeQuery(id+"F12.imprint","IMPRINT",EDGE,{"derivedFrom":subQ0}),1.0]])]});}
            var Q6;
            {var subQ0=sQuery(id+"F12.wireOp",EDGE,"E87");var subQ1=sQuery(id+"F12.wireOp",EDGE,"E84.right");var subQ2=makeQuery(id+"F12.imprint","INTERSECT",VERTEX,{"derivedFrom":[subQ1,subQ0]});Q6=makeQuery(id+"F12.imprint","IMPRINT",FACE,{"disambiguationData":[TD([[makeQuery(id+"F12.imprint","IMPRINT",EDGE,{"disambiguationData":[TD([[subQ2,-1.0]])],"derivedFrom":subQ1}),-1.0]])]});}
            var Q7;
            {var subQ1=sQuery(id+"F12.wireOp",EDGE,"E57.left");var subQ3=sQuery(id+"F12.wireOp",EDGE,"E62");var subQ4=makeQuery(id+"F12.imprint","INTERSECT",VERTEX,{"derivedFrom":[subQ1,subQ3]});Q7=makeQuery(id+"F12.imprint","IMPRINT",FACE,{"disambiguationData":[TD([[makeQuery(id+"F12.imprint","IMPRINT",EDGE,{"disambiguationData":[TD([[subQ4,1.0]])],"derivedFrom":subQ1}),1.0]])]});}
            var Q8;
            {var subQ0=sQuery(id+"F12.wireOp",EDGE,"E58");Q8=makeQuery(id+"F12.imprint","IMPRINT",FACE,{"disambiguationData":[TD([[makeQuery(id+"F12.imprint","IMPRINT",EDGE,{"derivedFrom":subQ0}),-1.0]])]});}
            var Q9;
            {var subQ1=sQuery(id+"F12.wireOp",EDGE,"E57.bottom");var subQ3=sQuery(id+"F12.wireOp",EDGE,"E63");var subQ4=makeQuery(id+"F12.imprint","INTERSECT",VERTEX,{"derivedFrom":[subQ1,subQ3]});Q9=makeQuery(id+"F12.imprint","IMPRINT",FACE,{"disambiguationData":[TD([[makeQuery(id+"F12.imprint","IMPRINT",EDGE,{"disambiguationData":[TD([[subQ4,-1.0]])],"derivedFrom":subQ3}),-1.0]])]});}
            var Q10;
            {var subQ0=sQuery(id+"F12.wireOp",EDGE,"E62");var subQ1=sQuery(id+"F12.wireOp",EDGE,"E57.bottom");var subQ2=makeQuery(id+"F12.imprint","INTERSECT",VERTEX,{"derivedFrom":[subQ1,subQ0]});Q10=makeQuery(id+"F12.imprint","IMPRINT",FACE,{"disambiguationData":[TD([[makeQuery(id+"F12.imprint","IMPRINT",EDGE,{"disambiguationData":[TD([[subQ2,1.0]])],"derivedFrom":subQ1}),-1.0]])]});}
            var Q11;
            {var subQ0=sQuery(id+"F12.wireOp",EDGE,"E63");var subQ1=sQuery(id+"F12.wireOp",EDGE,"E62");var subQ2=makeQuery(id+"F12.imprint","INTERSECT",VERTEX,{"derivedFrom":[subQ1,subQ0]});Q11=makeQuery(id+"F12.imprint","IMPRINT",FACE,{"disambiguationData":[TD([[makeQuery(id+"F12.imprint","IMPRINT",EDGE,{"disambiguationData":[TD([[subQ2,1.0]])],"derivedFrom":subQ1}),-1.0]])]});}
            var Q12;
            {var subQ1=sQuery(id+"F12.wireOp",EDGE,"E57.bottom");var subQ3=sQuery(id+"F12.wireOp",EDGE,"E62");var subQ4=makeQuery(id+"F12.imprint","INTERSECT",VERTEX,{"derivedFrom":[subQ1,subQ3]});Q12=makeQuery(id+"F12.imprint","IMPRINT",FACE,{"disambiguationData":[TD([[makeQuery(id+"F12.imprint","IMPRINT",EDGE,{"disambiguationData":[TD([[subQ4,1.0]])],"derivedFrom":subQ3}),-1.0]])]});}
            var Q13;
            {var subQ0=sQuery(id+"F12.wireOp",EDGE,"E59");Q13=makeQuery(id+"F12.imprint","IMPRINT",FACE,{"disambiguationData":[TD([[makeQuery(id+"F12.imprint","IMPRINT",EDGE,{"derivedFrom":subQ0}),-1.0]])]});}
            var Q14;
            {var subQ1=sQuery(id+"F12.wireOp",EDGE,"E57.right");var subQ3=sQuery(id+"F12.wireOp",EDGE,"E63");var subQ4=makeQuery(id+"F12.imprint","INTERSECT",VERTEX,{"derivedFrom":[subQ1,subQ3]});Q14=makeQuery(id+"F12.imprint","IMPRINT",FACE,{"disambiguationData":[TD([[makeQuery(id+"F12.imprint","IMPRINT",EDGE,{"disambiguationData":[TD([[subQ4,1.0]])],"derivedFrom":subQ1}),-1.0]])]});}
            var Q15;
            {var subQ1=sQuery(id+"F12.wireOp",EDGE,"E57.left");var subQ3=sQuery(id+"F12.wireOp",EDGE,"E62");var subQ4=makeQuery(id+"F12.imprint","INTERSECT",VERTEX,{"derivedFrom":[subQ1,subQ3]});Q15=makeQuery(id+"F12.imprint","IMPRINT",FACE,{"disambiguationData":[TD([[makeQuery(id+"F12.imprint","IMPRINT",EDGE,{"disambiguationData":[TD([[subQ4,-1.0]])],"derivedFrom":subQ1}),1.0]])]});}
            var Q16;
            {var subQ0=sQuery(id+"F12.wireOp",EDGE,"E74");Q16=makeQuery(id+"F12.imprint","IMPRINT",FACE,{"disambiguationData":[TD([[makeQuery(id+"F12.imprint","IMPRINT",EDGE,{"derivedFrom":subQ0}),-1.0]])]});}
            var Q17;
            {var subQ0=sQuery(id+"F12.wireOp",EDGE,"E60");Q17=makeQuery(id+"F12.imprint","IMPRINT",FACE,{"disambiguationData":[TD([[makeQuery(id+"F12.imprint","IMPRINT",EDGE,{"derivedFrom":subQ0}),1.0]])]});}
            var Q18;
            {var subQ0=sQuery(id+"F12.wireOp",EDGE,"E57.top");Q18=makeQuery(id+"F12.imprint","IMPRINT",FACE,{"disambiguationData":[TD([[makeQuery(id+"F12.imprint","IMPRINT",EDGE,{"derivedFrom":subQ0}),1.0]])]});}
            var Q19;
            {var subQ0=sQuery(id+"F12.wireOp",EDGE,"E75");var subQ1=sQuery(id+"F12.wireOp",EDGE,"E64");var subQ2=makeQuery(id+"F12.imprint","INTERSECT",VERTEX,{"derivedFrom":[subQ1,subQ0]});Q19=makeQuery(id+"F12.imprint","IMPRINT",FACE,{"disambiguationData":[TD([[makeQuery(id+"F12.imprint","IMPRINT",EDGE,{"disambiguationData":[TD([[subQ2,1.0]])],"derivedFrom":subQ1}),-1.0]])]});}
            var Q20;
            {var subQ0=sQuery(id+"F12.wireOp",EDGE,"E65");var subQ1=sQuery(id+"F12.wireOp",EDGE,"E64");var subQ2=makeQuery(id+"F12.imprint","INTERSECT",VERTEX,{"derivedFrom":[subQ1,subQ0]});Q20=makeQuery(id+"F12.imprint","IMPRINT",FACE,{"disambiguationData":[TD([[makeQuery(id+"F12.imprint","IMPRINT",EDGE,{"disambiguationData":[TD([[subQ2,1.0]])],"derivedFrom":subQ1}),1.0]])]});}
            var Q21;
            {var subQ0=sQuery(id+"F12.wireOp",EDGE,"E75");var subQ1=sQuery(id+"F12.wireOp",EDGE,"E64");var subQ2=makeQuery(id+"F12.imprint","INTERSECT",VERTEX,{"derivedFrom":[subQ1,subQ0]});Q21=makeQuery(id+"F12.imprint","IMPRINT",FACE,{"disambiguationData":[TD([[makeQuery(id+"F12.imprint","IMPRINT",EDGE,{"disambiguationData":[TD([[subQ2,1.0]])],"derivedFrom":subQ1}),1.0]])]});}
            var Q22;
            {var subQ0=sQuery(id+"F12.wireOp",EDGE,"E61");Q22=makeQuery(id+"F12.imprint","IMPRINT",FACE,{"disambiguationData":[TD([[makeQuery(id+"F12.imprint","IMPRINT",EDGE,{"derivedFrom":subQ0}),1.0]])]});}
            var Q23;
            {var subQ0=sQuery(id+"F12.wireOp",EDGE,"E63");var subQ1=sQuery(id+"F12.wireOp",EDGE,"E57.right");var subQ2=makeQuery(id+"F12.imprint","INTERSECT",VERTEX,{"derivedFrom":[subQ1,subQ0]});Q23=makeQuery(id+"F12.imprint","IMPRINT",FACE,{"disambiguationData":[TD([[makeQuery(id+"F12.imprint","IMPRINT",EDGE,{"disambiguationData":[TD([[subQ2,-1.0]])],"derivedFrom":subQ1}),-1.0]])]});}
            var Q24;
            {var subQ1=sQuery(id+"F12.wireOp",EDGE,"E57.right");var subQ3=sQuery(id+"F12.wireOp",EDGE,"E65");var subQ4=makeQuery(id+"F12.imprint","INTERSECT",VERTEX,{"derivedFrom":[subQ1,subQ3]});Q24=makeQuery(id+"F12.imprint","IMPRINT",FACE,{"disambiguationData":[TD([[makeQuery(id+"F12.imprint","IMPRINT",EDGE,{"disambiguationData":[TD([[subQ4,-1.0]])],"derivedFrom":subQ1}),-1.0]])]});}
            var Q25;
            {var subQ0=sQuery(id+"F12.wireOp",EDGE,"E76.left");var subQ1=sQuery(id+"F12.wireOp",EDGE,"E76.bottom");var subQ2=makeQuery(id+"F12.imprint","INTERSECT",VERTEX,{"derivedFrom":[subQ1,subQ0]});Q25=makeQuery(id+"F12.imprint","IMPRINT",FACE,{"disambiguationData":[TD([[makeQuery(id+"F12.imprint","IMPRINT",EDGE,{"disambiguationData":[TD([[subQ2,-1.0]])],"derivedFrom":subQ1}),-1.0]])]});}
            var Q26;
            {var subQ1=sQuery(id+"F12.wireOp",EDGE,"E76.bottom");var subQ3=sQuery(id+"F12.wireOp",EDGE,"E77");var subQ4=makeQuery(id+"F12.imprint","INTERSECT",VERTEX,{"derivedFrom":[subQ1,subQ3]});Q26=makeQuery(id+"F12.imprint","IMPRINT",FACE,{"disambiguationData":[TD([[makeQuery(id+"F12.imprint","IMPRINT",EDGE,{"disambiguationData":[TD([[subQ4,-1.0]])],"derivedFrom":subQ3}),1.0]])]});}
            var Q27;
            {var subQ0=sQuery(id+"F12.wireOp",EDGE,"E79");Q27=makeQuery(id+"F12.imprint","IMPRINT",FACE,{"disambiguationData":[TD([[makeQuery(id+"F12.imprint","IMPRINT",EDGE,{"derivedFrom":subQ0}),-1.0]])]});}
            var Q28;
            {var subQ0=sQuery(id+"F12.wireOp",EDGE,"E78");var subQ1=sQuery(id+"F12.wireOp",EDGE,"E76.left");var subQ2=makeQuery(id+"F12.imprint","INTERSECT",VERTEX,{"derivedFrom":[subQ1,subQ0]});Q28=makeQuery(id+"F12.imprint","IMPRINT",FACE,{"disambiguationData":[TD([[makeQuery(id+"F12.imprint","IMPRINT",EDGE,{"disambiguationData":[TD([[subQ2,-1.0]])],"derivedFrom":subQ1}),1.0]])]});}
            var Q29;
            {var subQ0=sQuery(id+"F12.wireOp",EDGE,"E76.right");Q29=makeQuery(id+"F12.imprint","IMPRINT",FACE,{"disambiguationData":[TD([[makeQuery(id+"F12.imprint","IMPRINT",EDGE,{"derivedFrom":subQ0}),-1.0]])]});}
            var Q30;
            {var subQ0=sQuery(id+"F12.wireOp",EDGE,"E80");var subQ1=sQuery(id+"F12.wireOp",EDGE,"E76.left");var subQ2=makeQuery(id+"F12.imprint","INTERSECT",VERTEX,{"derivedFrom":[subQ1,subQ0]});Q30=makeQuery(id+"F12.imprint","IMPRINT",FACE,{"disambiguationData":[TD([[makeQuery(id+"F12.imprint","IMPRINT",EDGE,{"disambiguationData":[TD([[subQ2,1.0]])],"derivedFrom":subQ1}),1.0]])]});}
            var Q31;
            {var subQ0=sQuery(id+"F12.wireOp",EDGE,"E81");var subQ1=sQuery(id+"F12.wireOp",EDGE,"E77");var subQ2=makeQuery(id+"F12.imprint","INTERSECT",VERTEX,{"derivedFrom":[subQ1,subQ0]});Q31=makeQuery(id+"F12.imprint","IMPRINT",FACE,{"disambiguationData":[TD([[makeQuery(id+"F12.imprint","IMPRINT",EDGE,{"disambiguationData":[TD([[subQ2,-1.0]])],"derivedFrom":subQ1}),1.0]])]});}
            var Q32;
            {var subQ0=sQuery(id+"F12.wireOp",EDGE,"E83");Q32=makeQuery(id+"F12.imprint","IMPRINT",FACE,{"disambiguationData":[TD([[makeQuery(id+"F12.imprint","IMPRINT",EDGE,{"derivedFrom":subQ0}),1.0]])]});}
            var Q33;
            {var subQ0=sQuery(id+"F12.wireOp",EDGE,"E76.top");Q33=makeQuery(id+"F12.imprint","IMPRINT",FACE,{"disambiguationData":[TD([[makeQuery(id+"F12.imprint","IMPRINT",EDGE,{"derivedFrom":subQ0}),1.0]])]});}
            var Q34;
            {var subQ0=sQuery(id+"F12.wireOp",EDGE,"E91.left");var subQ1=sQuery(id+"F12.wireOp",EDGE,"E91.bottom");var subQ2=makeQuery(id+"F12.imprint","INTERSECT",VERTEX,{"derivedFrom":[subQ1,subQ0]});Q34=makeQuery(id+"F12.imprint","IMPRINT",FACE,{"disambiguationData":[TD([[makeQuery(id+"F12.imprint","IMPRINT",EDGE,{"disambiguationData":[TD([[subQ2,-1.0]])],"derivedFrom":subQ1}),-1.0]])]});}
            var Q35;
            {var subQ0=sQuery(id+"F12.wireOp",EDGE,"E91.right");Q35=makeQuery(id+"F12.imprint","IMPRINT",FACE,{"disambiguationData":[TD([[makeQuery(id+"F12.imprint","IMPRINT",EDGE,{"derivedFrom":subQ0}),-1.0]])]});}
            var Q36;
            {var subQ0=sQuery(id+"F12.wireOp",EDGE,"E93");var subQ1=sQuery(id+"F12.wireOp",EDGE,"E91.left");var subQ2=makeQuery(id+"F12.imprint","INTERSECT",VERTEX,{"derivedFrom":[subQ1,subQ0]});Q36=makeQuery(id+"F12.imprint","IMPRINT",FACE,{"disambiguationData":[TD([[makeQuery(id+"F12.imprint","IMPRINT",EDGE,{"disambiguationData":[TD([[subQ2,-1.0]])],"derivedFrom":subQ1}),1.0]])]});}
            var Q37;
            {var subQ0=sQuery(id+"F12.wireOp",EDGE,"E95");var subQ1=sQuery(id+"F12.wireOp",EDGE,"E91.left");var subQ2=makeQuery(id+"F12.imprint","INTERSECT",VERTEX,{"derivedFrom":[subQ1,subQ0]});Q37=makeQuery(id+"F12.imprint","IMPRINT",FACE,{"disambiguationData":[TD([[makeQuery(id+"F12.imprint","IMPRINT",EDGE,{"disambiguationData":[TD([[subQ2,-1.0]])],"derivedFrom":subQ1}),1.0]])]});}
            var Q38;
            {var subQ5=sQuery(id+"F12.wireOp",EDGE,"E97.trimOffspring");Q38=makeQuery(id+"F12.imprint","IMPRINT",FACE,{"disambiguationData":[TD([[makeQuery(id+"F12.imprint","IMPRINT",EDGE,{"derivedFrom":subQ5}),-1.0]])]});}
            var Q39;
            {var subQ0=sQuery(id+"F12.wireOp",EDGE,"E94");var subQ1=sQuery(id+"F12.wireOp",EDGE,"E91.left");var subQ2=makeQuery(id+"F12.imprint","INTERSECT",VERTEX,{"derivedFrom":[subQ1,subQ0]});Q39=makeQuery(id+"F12.imprint","IMPRINT",FACE,{"disambiguationData":[TD([[makeQuery(id+"F12.imprint","IMPRINT",EDGE,{"disambiguationData":[TD([[subQ2,1.0]])],"derivedFrom":subQ1}),1.0]])]});}
            var Q40;
            {var subQ0=sQuery(id+"F12.wireOp",EDGE,"E91.left");var subQ1=sQuery(id+"F12.wireOp",EDGE,"E91.top");var subQ2=makeQuery(id+"F12.imprint","INTERSECT",VERTEX,{"derivedFrom":[subQ1,subQ0]});Q40=makeQuery(id+"F12.imprint","IMPRINT",FACE,{"disambiguationData":[TD([[makeQuery(id+"F12.imprint","IMPRINT",EDGE,{"disambiguationData":[TD([[subQ2,-1.0]])],"derivedFrom":subQ1}),1.0]])]});}
            var Q41;
            {var subQ0=sQuery(id+"F12.wireOp",EDGE,"E98.trimOffspring");Q41=makeQuery(id+"F12.imprint","IMPRINT",FACE,{"disambiguationData":[TD([[makeQuery(id+"F12.imprint","IMPRINT",EDGE,{"derivedFrom":subQ0}),-1.0]])]});}
            extrude(context, id + "F13", {"entities" : qUnion([Q0, Q1, Q2, Q3, Q4, Q5, Q6, Q7, Q8, Q9, Q10, Q11, Q12, Q13, Q14, Q15, Q16, Q17, Q18, Q19, Q20, Q21, Q22, Q23, Q24, Q25, Q26, Q27, Q28, Q29, Q30, Q31, Q32, Q33, Q34, Q35, Q36, Q37, Q38, Q39, Q40, Q41]), "operationType" : NewBodyOperationType.ADD, "depth" : 1.27 * mm, "offsetDistance" : 25.4 * mm});
        }
        {
            var Q0;
            Q0=makeQuery(id+"F13.opExtrude","CAP_EDGE",EDGE,{"disambiguationData":[OSD([sQuery(id+"F12.wireOp",EDGE,"E84.top")])],"isStart":false});
            var Q1;
            Q1=makeQuery(id+"F13.opExtrude","CAP_EDGE",EDGE,{"disambiguationData":[OSD([sQuery(id+"F12.wireOp",EDGE,"E88")])],"isStart":false});
            var Q2;
            Q2=makeQuery(id+"F13.opExtrude","CAP_EDGE",EDGE,{"disambiguationData":[OSD([sQuery(id+"F12.wireOp",EDGE,"E90.trimOffspring")])],"isStart":false});
            var Q3;
            Q3=makeQuery(id+"F13.opExtrude","CAP_EDGE",EDGE,{"disambiguationData":[OSD([sQuery(id+"F12.wireOp",EDGE,"E57.top"),sQuery(id+"F12.wireOp",EDGE,"E75")])],"isStart":false});
            var Q4;
            Q4=makeQuery(id+"F13.opExtrude","CAP_EDGE",EDGE,{"disambiguationData":[OSD([sQuery(id+"F12.wireOp",EDGE,"E76.top")])],"isStart":false});
            var Q5;
            Q5=makeQuery(id+"F13.opExtrude","CAP_EDGE",EDGE,{"disambiguationData":[OSD([sQuery(id+"F12.wireOp",EDGE,"E80")])],"isStart":false});
            var Q6;
            Q6=makeQuery(id+"F13.opExtrude","CAP_EDGE",EDGE,{"disambiguationData":[OSD([sQuery(id+"F12.wireOp",EDGE,"E66")])],"isStart":false});
            var Q7;
            Q7=makeQuery(id+"F13.opExtrude","CAP_EDGE",EDGE,{"disambiguationData":[OSD([sQuery(id+"F12.wireOp",EDGE,"E78")])],"isStart":false});
            var Q8;
            Q8=makeQuery(id+"F13.opExtrude","CAP_EDGE",EDGE,{"disambiguationData":[OSD([sQuery(id+"F12.wireOp",EDGE,"E91.top")])],"isStart":false});
            var Q9;
            Q9=makeQuery(id+"F13.opExtrude","CAP_EDGE",EDGE,{"disambiguationData":[OSD([sQuery(id+"F12.wireOp",EDGE,"E96")])],"isStart":false});
            var Q10;
            Q10=makeQuery(id+"F13.opExtrude","CAP_EDGE",EDGE,{"disambiguationData":[OSD([sQuery(id+"F12.wireOp",EDGE,"E93")])],"isStart":false});
            chamfer(context, id + "F14", {"entities" : qUnion([Q0, Q1, Q2, Q3, Q4, Q5, Q6, Q7, Q8, Q9, Q10]), "width" : 1.27 * mm, "tangentPropagation" : true});
        }
        {
            var Q0;
            Q0=makeQuery(id+"F1.opExtrude","SWEPT_FACE",FACE,{"disambiguationData":[OSD([sQuery(id+"F0.wireOp",EDGE,"E0.top")])]});
            var sketch = newSketch(context, id + "F15", { "sketchPlane" : qUnion([Q0])});
            skLineSegment(sketch, "E99", {"start": v(4.78, -2.64) * mm, "end": v(55.55, -2.64) * mm});
            skLineSegment(sketch, "E100", {"start": v(55.55, -2.64) * mm, "end": v(55.55, -3.7) * mm});
            skLineSegment(sketch, "E101", {"start": v(55.55, -3.7) * mm, "end": v(4.78, -3.7) * mm});
            skLineSegment(sketch, "E102", {"start": v(4.78, -3.7) * mm, "end": v(4.78, -2.64) * mm});
            skSolve(sketch);
        }
        {
            var Q0;
            {var subQ2=sQuery(id+"F15.wireOp",EDGE,"E102");Q0=makeQuery(id+"F15.imprint","IMPRINT",FACE,{"disambiguationData":[TD([[makeQuery(id+"F15.imprint","IMPRINT",EDGE,{"derivedFrom":subQ2}),1.0]])]});}
            var Q1;
            {var subQ1=makeQuery(id+"F3.boolean.opBoolean","COPY",EDGE,{"derivedFrom":makeQuery(id+"F3.opExtrude","CAP_EDGE",EDGE,{"disambiguationData":[OSD([sQuery(id+"F2.wireOp",EDGE,"E5")])],"isStart":true})});Q1=makeQuery(id+"F15.imprint","IMPRINT",FACE,{"disambiguationData":[TD([[makeQuery(id+"F15.imprint","IMPRINT",EDGE,{"derivedFrom":subQ1}),1.0]])]});}
            var Q2;
            {var subQ2=sQuery(id+"F15.wireOp",EDGE,"E100");Q2=makeQuery(id+"F15.imprint","IMPRINT",FACE,{"disambiguationData":[TD([[makeQuery(id+"F15.imprint","IMPRINT",EDGE,{"derivedFrom":subQ2}),1.0]])]});}
            extrude(context, id + "F16", {"entities" : qUnion([Q0, Q1, Q2]), "operationType" : NewBodyOperationType.REMOVE, "oppositeDirection" : true, "depth" : 3.17 * mm, "offsetDistance" : 25.4 * mm});
        }
        {
            var Q0;
            Q0=makeQuery(id+"F1.opExtrude","SWEPT_FACE",FACE,{"disambiguationData":[OSD([sQuery(id+"F0.wireOp",EDGE,"E0.bottom")])]});
            var sketch = newSketch(context, id + "F17", { "sketchPlane" : qUnion([Q0])});
            skLineSegment(sketch, "E103.bottom", {"start": v(55.55, 3.7) * mm, "end": v(56.62, 3.7) * mm});
            skLineSegment(sketch, "E103.top", {"start": v(55.55, 2.64) * mm, "end": v(56.62, 2.64) * mm});
            skLineSegment(sketch, "E103.left", {"start": v(55.55, 3.7) * mm, "end": v(55.55, 2.64) * mm});
            skLineSegment(sketch, "E103.right", {"start": v(56.62, 3.7) * mm, "end": v(56.62, 3.43) * mm});
            skLineSegment(sketch, "E104", {"start": v(56.08, 3.7) * mm, "end": v(56.08, 3.7) * mm});
            skArc(sketch, "E105", {"start": v(56.55, 3.43) * mm, "mid": v(55.55, 3.17) * mm, "end": v(56.55, 2.92) * mm});
            skLineSegment(sketch, "E106", {"start": v(55.55, 3.18) * mm, "end": v(55.55, 3.18) * mm});
            skLineSegment(sketch, "E107.trimOffspring", {"start": v(56.08, 2.64) * mm, "end": v(56.08, 2.64) * mm});
            skLineSegment(sketch, "E108.trimOffspring", {"start": v(56.62, 2.92) * mm, "end": v(56.62, 2.64) * mm});
            skLineSegment(sketch, "E109.trimOffspring", {"start": v(56.55, 2.92) * mm, "end": v(56.62, 2.92) * mm});
            skLineSegment(sketch, "E110.trimOffspring", {"start": v(56.55, 3.43) * mm, "end": v(56.62, 3.43) * mm});
            skLineSegment(sketch, "E111.bottom", {"start": v(46.15, 3.7) * mm, "end": v(45.09, 3.7) * mm});
            skLineSegment(sketch, "E111.top", {"start": v(46.15, 2.64) * mm, "end": v(45.09, 2.64) * mm});
            skLineSegment(sketch, "E111.left", {"start": v(46.15, 3.7) * mm, "end": v(46.15, 2.64) * mm});
            skLineSegment(sketch, "E111.right", {"start": v(45.09, 3.7) * mm, "end": v(45.09, 3.43) * mm});
            skLineSegment(sketch, "E112", {"start": v(45.09, 3.18) * mm, "end": v(45.09, 3.18) * mm});
            skArc(sketch, "E113", {"start": v(45.15, 2.92) * mm, "mid": v(46.15, 3.18) * mm, "end": v(45.15, 3.43) * mm});
            skLineSegment(sketch, "E114", {"start": v(45.09, 3.43) * mm, "end": v(45.15, 3.43) * mm});
            skLineSegment(sketch, "E115", {"start": v(45.09, 2.92) * mm, "end": v(45.15, 2.92) * mm});
            skLineSegment(sketch, "E116.trimOffspring", {"start": v(45.09, 2.92) * mm, "end": v(45.09, 2.64) * mm});
            skLineSegment(sketch, "E117.trimOffspring", {"start": v(46.15, 3.18) * mm, "end": v(46.15, 3.18) * mm});
            skLineSegment(sketch, "E118.bottom", {"start": v(34.86, 3.7) * mm, "end": v(35.93, 3.7) * mm});
            skLineSegment(sketch, "E118.top", {"start": v(34.86, 2.64) * mm, "end": v(35.93, 2.64) * mm});
            skLineSegment(sketch, "E118.left", {"start": v(34.86, 3.7) * mm, "end": v(34.86, 2.64) * mm});
            skLineSegment(sketch, "E118.right", {"start": v(35.93, 3.7) * mm, "end": v(35.93, 3.43) * mm});
            skLineSegment(sketch, "E119", {"start": v(34.86, 3.18) * mm, "end": v(34.86, 3.18) * mm});
            skArc(sketch, "E120", {"start": v(35.86, 3.43) * mm, "mid": v(34.86, 3.18) * mm, "end": v(35.86, 2.92) * mm});
            skLineSegment(sketch, "E121.trimOffspring", {"start": v(35.86, 3.43) * mm, "end": v(35.93, 3.43) * mm});
            skLineSegment(sketch, "E122.trimOffspring", {"start": v(35.93, 3.18) * mm, "end": v(35.93, 3.18) * mm});
            skLineSegment(sketch, "E123.trimOffspring", {"start": v(35.86, 2.92) * mm, "end": v(35.93, 2.92) * mm});
            skLineSegment(sketch, "E124.trimOffspring", {"start": v(35.93, 2.92) * mm, "end": v(35.93, 2.64) * mm});
            skLineSegment(sketch, "E125.bottom", {"start": v(25.46, 3.7) * mm, "end": v(24.4, 3.7) * mm});
            skLineSegment(sketch, "E125.top", {"start": v(25.46, 2.64) * mm, "end": v(24.4, 2.64) * mm});
            skLineSegment(sketch, "E125.left", {"start": v(25.46, 3.7) * mm, "end": v(25.46, 2.64) * mm});
            skLineSegment(sketch, "E125.right", {"start": v(24.4, 3.7) * mm, "end": v(24.4, 3.43) * mm});
            skArc(sketch, "E126", {"start": v(24.46, 2.92) * mm, "mid": v(25.46, 3.18) * mm, "end": v(24.46, 3.43) * mm});
            skLineSegment(sketch, "E127", {"start": v(24.4, 3.43) * mm, "end": v(24.46, 3.43) * mm});
            skLineSegment(sketch, "E128", {"start": v(24.4, 2.92) * mm, "end": v(24.46, 2.92) * mm});
            skLineSegment(sketch, "E129.trimOffspring", {"start": v(24.4, 2.92) * mm, "end": v(24.4, 2.64) * mm});
            skPoint(sketch, "E130.orphan", {"position": v(24.4, 3.18) * mm});
            skPoint(sketch, "E131.end.orphan", {"position": v(25.46, 3.18) * mm});
            skLineSegment(sketch, "E132.bottom", {"start": v(14.17, 3.7) * mm, "end": v(15.24, 3.7) * mm});
            skLineSegment(sketch, "E132.top", {"start": v(14.17, 2.64) * mm, "end": v(15.24, 2.64) * mm});
            skLineSegment(sketch, "E132.left", {"start": v(14.17, 3.7) * mm, "end": v(14.17, 2.64) * mm});
            skLineSegment(sketch, "E132.right", {"start": v(15.24, 3.7) * mm, "end": v(15.24, 3.43) * mm});
            skArc(sketch, "E133", {"start": v(15.18, 3.43) * mm, "mid": v(14.17, 3.18) * mm, "end": v(15.18, 2.92) * mm});
            skLineSegment(sketch, "E134.trimOffspring", {"start": v(15.24, 2.92) * mm, "end": v(15.24, 2.64) * mm});
            skLineSegment(sketch, "E135.trimOffspring", {"start": v(15.18, 3.43) * mm, "end": v(15.24, 3.43) * mm});
            skPoint(sketch, "E136.start.orphan", {"position": v(14.17, 3.18) * mm});
            skPoint(sketch, "E137.orphan", {"position": v(15.24, 3.18) * mm});
            skLineSegment(sketch, "E138.trimOffspring", {"start": v(15.18, 2.92) * mm, "end": v(15.24, 2.92) * mm});
            skLineSegment(sketch, "E139.bottom", {"start": v(4.78, 3.7) * mm, "end": v(3.7, 3.7) * mm});
            skLineSegment(sketch, "E139.top", {"start": v(4.78, 2.64) * mm, "end": v(3.7, 2.64) * mm});
            skLineSegment(sketch, "E139.left", {"start": v(4.78, 3.7) * mm, "end": v(4.78, 2.64) * mm});
            skLineSegment(sketch, "E139.right", {"start": v(3.7, 3.7) * mm, "end": v(3.7, 3.43) * mm});
            skLineSegment(sketch, "E140.trimOffspring", {"start": v(3.7, 2.92) * mm, "end": v(3.7, 2.64) * mm});
            skPoint(sketch, "E141.orphan", {"position": v(3.7, 3.18) * mm});
            skPoint(sketch, "E142.end.orphan", {"position": v(4.78, 3.18) * mm});
            skLineSegment(sketch, "E143", {"start": v(4.77, 3.18) * mm, "end": v(4.78, 3.18) * mm});
            skArc(sketch, "E144", {"start": v(3.78, 2.92) * mm, "mid": v(4.77, 3.18) * mm, "end": v(3.78, 3.43) * mm});
            skLineSegment(sketch, "E145", {"start": v(3.7, 3.43) * mm, "end": v(3.78, 3.43) * mm});
            skLineSegment(sketch, "E146", {"start": v(3.7, 2.92) * mm, "end": v(3.78, 2.92) * mm});
            skSolve(sketch);
        }
        {
            var Q0;
            {var subQ0=sQuery(id+"F17.wireOp",EDGE,"E104");Q0=makeQuery(id+"F17.imprint","IMPRINT",FACE,{"disambiguationData":[TD([[makeQuery(id+"F17.imprint","IMPRINT",EDGE,{"derivedFrom":subQ0}),-1.0]])]});}
            var Q1;
            {var subQ0=sQuery(id+"F17.wireOp",EDGE,"E106");Q1=makeQuery(id+"F17.imprint","IMPRINT",FACE,{"disambiguationData":[TD([[makeQuery(id+"F17.imprint","IMPRINT",EDGE,{"derivedFrom":subQ0}),-1.0]])]});}
            var Q2;
            {var subQ2=sQuery(id+"F17.wireOp",EDGE,"E107.trimOffspring");Q2=makeQuery(id+"F17.imprint","IMPRINT",FACE,{"disambiguationData":[TD([[makeQuery(id+"F17.imprint","IMPRINT",EDGE,{"derivedFrom":subQ2}),1.0]])]});}
            var Q3;
            {var subQ3=sQuery(id+"F17.wireOp",EDGE,"E103.right");Q3=makeQuery(id+"F17.imprint","IMPRINT",FACE,{"disambiguationData":[TD([[makeQuery(id+"F17.imprint","IMPRINT",EDGE,{"derivedFrom":subQ3}),-1.0]])]});}
            var Q4;
            {var subQ4=sQuery(id+"F17.wireOp",EDGE,"E111.top");Q4=makeQuery(id+"F17.imprint","IMPRINT",FACE,{"disambiguationData":[TD([[makeQuery(id+"F17.imprint","IMPRINT",EDGE,{"derivedFrom":subQ4}),1.0]])]});}
            var Q5;
            {var subQ4=sQuery(id+"F17.wireOp",EDGE,"E111.bottom");Q5=makeQuery(id+"F17.imprint","IMPRINT",FACE,{"disambiguationData":[TD([[makeQuery(id+"F17.imprint","IMPRINT",EDGE,{"derivedFrom":subQ4}),-1.0]])]});}
            var Q6;
            {var subQ1=sQuery(id+"F17.wireOp",EDGE,"E118.bottom");Q6=makeQuery(id+"F17.imprint","IMPRINT",FACE,{"disambiguationData":[TD([[makeQuery(id+"F17.imprint","IMPRINT",EDGE,{"derivedFrom":subQ1}),-1.0]])]});}
            var Q7;
            {var subQ4=sQuery(id+"F17.wireOp",EDGE,"E118.top");Q7=makeQuery(id+"F17.imprint","IMPRINT",FACE,{"disambiguationData":[TD([[makeQuery(id+"F17.imprint","IMPRINT",EDGE,{"derivedFrom":subQ4}),1.0]])]});}
            var Q8;
            {var subQ0=sQuery(id+"F17.wireOp",EDGE,"E125.left");var subQ1=sQuery(id+"F17.wireOp",EDGE,"E125.bottom");var subQ2=makeQuery(id+"F17.imprint","INTERSECT",VERTEX,{"derivedFrom":[subQ1,subQ0]});Q8=makeQuery(id+"F17.imprint","IMPRINT",FACE,{"disambiguationData":[TD([[makeQuery(id+"F17.imprint","IMPRINT",EDGE,{"disambiguationData":[TD([[subQ2,1.0]])],"derivedFrom":subQ1}),-1.0]])]});}
            var Q9;
            {var subQ0=sQuery(id+"F17.wireOp",EDGE,"E125.left");var subQ1=sQuery(id+"F17.wireOp",EDGE,"E125.top");var subQ2=makeQuery(id+"F17.imprint","INTERSECT",VERTEX,{"derivedFrom":[subQ1,subQ0]});Q9=makeQuery(id+"F17.imprint","IMPRINT",FACE,{"disambiguationData":[TD([[makeQuery(id+"F17.imprint","IMPRINT",EDGE,{"disambiguationData":[TD([[subQ2,1.0]])],"derivedFrom":subQ1}),1.0]])]});}
            var Q10;
            {var subQ5=sQuery(id+"F17.wireOp",EDGE,"E128");Q10=makeQuery(id+"F17.imprint","IMPRINT",FACE,{"disambiguationData":[TD([[makeQuery(id+"F17.imprint","IMPRINT",EDGE,{"derivedFrom":subQ5}),-1.0]])]});}
            var Q11;
            {var subQ0=sQuery(id+"F17.wireOp",EDGE,"E125.right");Q11=makeQuery(id+"F17.imprint","IMPRINT",FACE,{"disambiguationData":[TD([[makeQuery(id+"F17.imprint","IMPRINT",EDGE,{"derivedFrom":subQ0}),1.0]])]});}
            var Q12;
            {var subQ0=sQuery(id+"F17.wireOp",EDGE,"E132.right");Q12=makeQuery(id+"F17.imprint","IMPRINT",FACE,{"disambiguationData":[TD([[makeQuery(id+"F17.imprint","IMPRINT",EDGE,{"derivedFrom":subQ0}),-1.0]])]});}
            var Q13;
            {var subQ0=sQuery(id+"F17.wireOp",EDGE,"E132.left");var subQ1=sQuery(id+"F17.wireOp",EDGE,"E132.bottom");var subQ2=makeQuery(id+"F17.imprint","INTERSECT",VERTEX,{"derivedFrom":[subQ1,subQ0]});Q13=makeQuery(id+"F17.imprint","IMPRINT",FACE,{"disambiguationData":[TD([[makeQuery(id+"F17.imprint","IMPRINT",EDGE,{"disambiguationData":[TD([[subQ2,-1.0]])],"derivedFrom":subQ1}),-1.0]])]});}
            var Q14;
            {var subQ0=sQuery(id+"F17.wireOp",EDGE,"E132.left");var subQ1=sQuery(id+"F17.wireOp",EDGE,"E132.top");var subQ2=makeQuery(id+"F17.imprint","INTERSECT",VERTEX,{"derivedFrom":[subQ1,subQ0]});Q14=makeQuery(id+"F17.imprint","IMPRINT",FACE,{"disambiguationData":[TD([[makeQuery(id+"F17.imprint","IMPRINT",EDGE,{"disambiguationData":[TD([[subQ2,-1.0]])],"derivedFrom":subQ1}),1.0]])]});}
            var Q15;
            {var subQ0=sQuery(id+"F17.wireOp",EDGE,"E134.trimOffspring");Q15=makeQuery(id+"F17.imprint","IMPRINT",FACE,{"disambiguationData":[TD([[makeQuery(id+"F17.imprint","IMPRINT",EDGE,{"derivedFrom":subQ0}),-1.0]])]});}
            var Q16;
            {var subQ1=sQuery(id+"F17.wireOp",EDGE,"E139.bottom");var subQ8=sQuery(id+"F17.wireOp",EDGE,"vViUwkOb-oigo-wygR-mELl-0DaQxFGob972");var subQ9=makeQuery(id+"F17.imprint","INTERSECT",VERTEX,{"derivedFrom":[subQ1,subQ8]});Q16=makeQuery(id+"F17.imprint","IMPRINT",FACE,{"disambiguationData":[TD([[makeQuery(id+"F17.imprint","IMPRINT",EDGE,{"disambiguationData":[TD([[subQ9,1.0]])],"derivedFrom":subQ8}),-1.0]])]});}
            var Q17;
            {var subQ1=sQuery(id+"F17.wireOp",EDGE,"E139.top");var subQ8=sQuery(id+"F17.wireOp",EDGE,"vViUwkOb-oigo-wygR-mELl-0DaQxFGob972");var subQ9=makeQuery(id+"F17.imprint","INTERSECT",VERTEX,{"derivedFrom":[subQ1,subQ8]});Q17=makeQuery(id+"F17.imprint","IMPRINT",FACE,{"disambiguationData":[TD([[makeQuery(id+"F17.imprint","IMPRINT",EDGE,{"disambiguationData":[TD([[subQ9,-1.0]])],"derivedFrom":subQ8}),-1.0]])]});}
            var Q18;
            {var subQ1=sQuery(id+"F17.wireOp",EDGE,"E139.bottom");var subQ8=sQuery(id+"F17.wireOp",EDGE,"4g7BjY2D-837m-m5MQ-NrB3-Du0UvO8V4jLu");var subQ9=makeQuery(id+"F17.imprint","INTERSECT",VERTEX,{"derivedFrom":[subQ1,subQ8]});Q18=makeQuery(id+"F17.imprint","IMPRINT",FACE,{"disambiguationData":[TD([[makeQuery(id+"F17.imprint","IMPRINT",EDGE,{"disambiguationData":[TD([[subQ9,1.0]])],"derivedFrom":subQ8}),-1.0]])]});}
            var Q19;
            {var subQ1=sQuery(id+"F17.wireOp",EDGE,"E139.top");var subQ8=sQuery(id+"F17.wireOp",EDGE,"4g7BjY2D-837m-m5MQ-NrB3-Du0UvO8V4jLu");var subQ9=makeQuery(id+"F17.imprint","INTERSECT",VERTEX,{"derivedFrom":[subQ1,subQ8]});Q19=makeQuery(id+"F17.imprint","IMPRINT",FACE,{"disambiguationData":[TD([[makeQuery(id+"F17.imprint","IMPRINT",EDGE,{"disambiguationData":[TD([[subQ9,-1.0]])],"derivedFrom":subQ8}),-1.0]])]});}
            var Q20;
            {var subQ0=sQuery(id+"F17.wireOp",EDGE,"E139.right");Q20=makeQuery(id+"F17.imprint","IMPRINT",FACE,{"disambiguationData":[TD([[makeQuery(id+"F17.imprint","IMPRINT",EDGE,{"derivedFrom":subQ0}),1.0]])]});}
            var Q21;
            {var subQ4=sQuery(id+"F17.wireOp",EDGE,"k5wNbRY5-FWuI-R7YJ-O7Hm-kdHTz7NwDN8z");Q21=makeQuery(id+"F17.imprint","IMPRINT",FACE,{"disambiguationData":[TD([[makeQuery(id+"F17.imprint","IMPRINT",EDGE,{"derivedFrom":subQ4}),-1.0]])]});}
            var Q22;
            {var subQ1=sQuery(id+"F17.wireOp",EDGE,"E139.top");Q22=makeQuery(id+"F17.imprint","IMPRINT",FACE,{"disambiguationData":[TD([[makeQuery(id+"F17.imprint","IMPRINT",EDGE,{"derivedFrom":subQ1}),-1.0]])]});}
            extrude(context, id + "F18", {"entities" : qUnion([Q0, Q1, Q2, Q3, Q4, Q5, Q6, Q7, Q8, Q9, Q10, Q11, Q12, Q13, Q14, Q15, Q16, Q17, Q18, Q19, Q20, Q21, Q22]), "operationType" : NewBodyOperationType.ADD, "oppositeDirection" : true, "depth" : 12.7 * mm, "offsetDistance" : 25.4 * mm});
        }
        {
            var Q0;
            {var subQ0=sQuery(id+"F0.wireOp",EDGE,"E0.bottom");var subQ2=sQuery(id+"F0.wireOp",EDGE,"E0.left");var subQ5=sQuery(id+"F2.wireOp",EDGE,"E2");var subQ6=makeQuery(id+"F3.opExtrude","SWEPT_FACE",FACE,{"disambiguationData":[OSD([subQ5]),TDD([makeQuery(id+"F2.imprint","IMPRINT",EDGE,{"disambiguationData":[TD([[makeQuery(id+"F2.imprint","INTERSECT",VERTEX,{"derivedFrom":[subQ5,sQuery(id+"F2.wireOp",EDGE,"E3")]}),1.0]])],"derivedFrom":subQ5})])]});var subQ7=makeQuery(id+"F1.opExtrude","SWEPT_FACE",FACE,{"disambiguationData":[OSD([subQ2])]});Q0=makeQuery(id+"F4.opChamfer","BLEND_EDGE",EDGE,{"blendedFrom":[makeQuery(id+"F3.boolean.opBoolean","SPLIT",EDGE,{"disambiguationData":[TD([subQ6])],"derivedFrom":makeQuery(id+"F1.opExtrude","SWEPT_EDGE",EDGE,{"disambiguationData":[OSD([subQ0,subQ2])]})}),makeQuery(id+"F3.boolean.opBoolean","SPLIT",FACE,{"disambiguationData":[TD([subQ6])],"derivedFrom":subQ7})],"blendedInto":[makeQuery(id+"F3.boolean.opBoolean","SPLIT",FACE,{"disambiguationData":[TD([subQ6])],"derivedFrom":subQ7})]});}
            var Q1;
            {var subQ0=sQuery(id+"F0.wireOp",EDGE,"E0.bottom");var subQ2=sQuery(id+"F2.wireOp",EDGE,"E1");var subQ3=sQuery(id+"F0.wireOp",EDGE,"E0.left");var subQ5=makeQuery(id+"F3.opExtrude","SWEPT_FACE",FACE,{"disambiguationData":[OSD([subQ2]),TDD([makeQuery(id+"F2.imprint","IMPRINT",EDGE,{"disambiguationData":[TD([[makeQuery(id+"F2.imprint","INTERSECT",VERTEX,{"derivedFrom":[subQ2,sQuery(id+"F2.wireOp",EDGE,"E3")]}),1.0]])],"derivedFrom":subQ2})])]});var subQ7=makeQuery(id+"F1.opExtrude","SWEPT_FACE",FACE,{"disambiguationData":[OSD([subQ3])]});Q1=makeQuery(id+"F4.opChamfer","BLEND_EDGE",EDGE,{"blendedFrom":[makeQuery(id+"F3.boolean.opBoolean","SPLIT",EDGE,{"disambiguationData":[TD([subQ5])],"derivedFrom":makeQuery(id+"F1.opExtrude","SWEPT_EDGE",EDGE,{"disambiguationData":[OSD([subQ0,subQ3])]})}),makeQuery(id+"F3.boolean.opBoolean","SPLIT",FACE,{"disambiguationData":[TD([subQ5])],"derivedFrom":subQ7})],"blendedInto":[makeQuery(id+"F3.boolean.opBoolean","SPLIT",FACE,{"disambiguationData":[TD([subQ5])],"derivedFrom":subQ7})]});}
            var Q2;
            {var subQ1=sQuery(id+"F2.wireOp",EDGE,"E1");var subQ2=sQuery(id+"F0.wireOp",EDGE,"E0.left");var subQ3=sQuery(id+"F0.wireOp",EDGE,"E0.top");var subQ4=makeQuery(id+"F1.opExtrude","SWEPT_EDGE",EDGE,{"disambiguationData":[OSD([subQ3,subQ2])]});var subQ5=makeQuery(id+"F3.opExtrude","SWEPT_FACE",FACE,{"disambiguationData":[OSD([subQ1]),TDD([makeQuery(id+"F2.imprint","IMPRINT",EDGE,{"disambiguationData":[TD([[makeQuery(id+"F2.imprint","INTERSECT",VERTEX,{"derivedFrom":[subQ1,sQuery(id+"F2.wireOp",EDGE,"E3")]}),1.0]])],"derivedFrom":subQ1})])]});var subQ8=makeQuery(id+"F1.opExtrude","SWEPT_FACE",FACE,{"disambiguationData":[OSD([subQ2])]});Q2=makeQuery(id+"F4.opChamfer","BLEND_EDGE",EDGE,{"blendedFrom":[makeQuery(id+"F3.boolean.opBoolean","SPLIT",EDGE,{"disambiguationData":[TD([subQ5])],"derivedFrom":subQ4}),makeQuery(id+"F3.boolean.opBoolean","SPLIT",FACE,{"disambiguationData":[TD([subQ5])],"derivedFrom":subQ8})],"blendedInto":[makeQuery(id+"F3.boolean.opBoolean","SPLIT",FACE,{"disambiguationData":[TD([subQ5])],"derivedFrom":subQ8})]});}
            var Q3;
            {var subQ1=sQuery(id+"F0.wireOp",EDGE,"E0.left");var subQ2=sQuery(id+"F0.wireOp",EDGE,"E0.top");var subQ4=sQuery(id+"F2.wireOp",EDGE,"E2");var subQ5=makeQuery(id+"F1.opExtrude","SWEPT_EDGE",EDGE,{"disambiguationData":[OSD([subQ2,subQ1])]});var subQ6=makeQuery(id+"F3.opExtrude","SWEPT_FACE",FACE,{"disambiguationData":[OSD([subQ4]),TDD([makeQuery(id+"F2.imprint","IMPRINT",EDGE,{"disambiguationData":[TD([[makeQuery(id+"F2.imprint","INTERSECT",VERTEX,{"derivedFrom":[subQ4,sQuery(id+"F2.wireOp",EDGE,"E3")]}),1.0]])],"derivedFrom":subQ4})])]});var subQ8=makeQuery(id+"F1.opExtrude","SWEPT_FACE",FACE,{"disambiguationData":[OSD([subQ1])]});Q3=makeQuery(id+"F4.opChamfer","BLEND_EDGE",EDGE,{"blendedFrom":[makeQuery(id+"F3.boolean.opBoolean","SPLIT",EDGE,{"disambiguationData":[TD([subQ6])],"derivedFrom":subQ5}),makeQuery(id+"F3.boolean.opBoolean","SPLIT",FACE,{"disambiguationData":[TD([subQ6])],"derivedFrom":subQ8})],"blendedInto":[makeQuery(id+"F3.boolean.opBoolean","SPLIT",FACE,{"disambiguationData":[TD([subQ6])],"derivedFrom":subQ8})]});}
            var Q4;
            {var subQ1=sQuery(id+"F0.wireOp",EDGE,"E0.right");var subQ2=sQuery(id+"F0.wireOp",EDGE,"E0.top");var subQ5=sQuery(id+"F2.wireOp",EDGE,"E1");var subQ6=makeQuery(id+"F1.opExtrude","SWEPT_EDGE",EDGE,{"disambiguationData":[OSD([subQ2,subQ1])]});var subQ7=makeQuery(id+"F3.opExtrude","SWEPT_FACE",FACE,{"disambiguationData":[OSD([subQ5]),TDD([makeQuery(id+"F2.imprint","IMPRINT",EDGE,{"disambiguationData":[TD([[makeQuery(id+"F2.imprint","INTERSECT",VERTEX,{"derivedFrom":[subQ5,sQuery(id+"F2.wireOp",EDGE,"E7")]}),-1.0]])],"derivedFrom":subQ5})])]});var subQ8=makeQuery(id+"F1.opExtrude","SWEPT_FACE",FACE,{"disambiguationData":[OSD([subQ1])]});Q4=makeQuery(id+"F4.opChamfer","BLEND_EDGE",EDGE,{"blendedFrom":[makeQuery(id+"F3.boolean.opBoolean","SPLIT",EDGE,{"disambiguationData":[TD([subQ7])],"derivedFrom":subQ6}),makeQuery(id+"F3.boolean.opBoolean","SPLIT",FACE,{"disambiguationData":[TD([subQ7])],"derivedFrom":subQ8})],"blendedInto":[makeQuery(id+"F3.boolean.opBoolean","SPLIT",FACE,{"disambiguationData":[TD([subQ7])],"derivedFrom":subQ8})]});}
            var Q5;
            {var subQ0=sQuery(id+"F0.wireOp",EDGE,"E0.bottom");var subQ2=sQuery(id+"F0.wireOp",EDGE,"E0.right");var subQ5=sQuery(id+"F2.wireOp",EDGE,"E1");var subQ6=makeQuery(id+"F3.opExtrude","SWEPT_FACE",FACE,{"disambiguationData":[OSD([subQ5]),TDD([makeQuery(id+"F2.imprint","IMPRINT",EDGE,{"disambiguationData":[TD([[makeQuery(id+"F2.imprint","INTERSECT",VERTEX,{"derivedFrom":[subQ5,sQuery(id+"F2.wireOp",EDGE,"E7")]}),-1.0]])],"derivedFrom":subQ5})])]});var subQ7=makeQuery(id+"F1.opExtrude","SWEPT_FACE",FACE,{"disambiguationData":[OSD([subQ2])]});Q5=makeQuery(id+"F4.opChamfer","BLEND_EDGE",EDGE,{"blendedFrom":[makeQuery(id+"F3.boolean.opBoolean","SPLIT",EDGE,{"disambiguationData":[TD([subQ6])],"derivedFrom":makeQuery(id+"F1.opExtrude","SWEPT_EDGE",EDGE,{"disambiguationData":[OSD([subQ0,subQ2])]})}),makeQuery(id+"F3.boolean.opBoolean","SPLIT",FACE,{"disambiguationData":[TD([subQ6])],"derivedFrom":subQ7})],"blendedInto":[makeQuery(id+"F3.boolean.opBoolean","SPLIT",FACE,{"disambiguationData":[TD([subQ6])],"derivedFrom":subQ7})]});}
            var Q6;
            {var subQ0=sQuery(id+"F0.wireOp",EDGE,"E0.bottom");var subQ2=sQuery(id+"F2.wireOp",EDGE,"E13.trimOffspring");var subQ3=sQuery(id+"F0.wireOp",EDGE,"E0.right");var subQ5=makeQuery(id+"F3.opExtrude","SWEPT_FACE",FACE,{"disambiguationData":[OSD([subQ2]),TDD([makeQuery(id+"F2.imprint","IMPRINT",EDGE,{"disambiguationData":[TD([[makeQuery(id+"F2.imprint","INTERSECT",VERTEX,{"derivedFrom":[sQuery(id+"F2.wireOp",EDGE,"E7"),subQ2]}),-1.0]])],"derivedFrom":subQ2})])]});var subQ7=makeQuery(id+"F1.opExtrude","SWEPT_FACE",FACE,{"disambiguationData":[OSD([subQ3])]});Q6=makeQuery(id+"F4.opChamfer","BLEND_EDGE",EDGE,{"blendedFrom":[makeQuery(id+"F3.boolean.opBoolean","SPLIT",EDGE,{"disambiguationData":[TD([subQ5])],"derivedFrom":makeQuery(id+"F1.opExtrude","SWEPT_EDGE",EDGE,{"disambiguationData":[OSD([subQ0,subQ3])]})}),makeQuery(id+"F3.boolean.opBoolean","SPLIT",FACE,{"disambiguationData":[TD([subQ5])],"derivedFrom":subQ7})],"blendedInto":[makeQuery(id+"F3.boolean.opBoolean","SPLIT",FACE,{"disambiguationData":[TD([subQ5])],"derivedFrom":subQ7})]});}
            var Q7;
            {var subQ1=sQuery(id+"F2.wireOp",EDGE,"E13.trimOffspring");var subQ2=sQuery(id+"F0.wireOp",EDGE,"E0.right");var subQ3=sQuery(id+"F0.wireOp",EDGE,"E0.top");var subQ4=makeQuery(id+"F1.opExtrude","SWEPT_EDGE",EDGE,{"disambiguationData":[OSD([subQ3,subQ2])]});var subQ5=makeQuery(id+"F3.opExtrude","SWEPT_FACE",FACE,{"disambiguationData":[OSD([subQ1]),TDD([makeQuery(id+"F2.imprint","IMPRINT",EDGE,{"disambiguationData":[TD([[makeQuery(id+"F2.imprint","INTERSECT",VERTEX,{"derivedFrom":[sQuery(id+"F2.wireOp",EDGE,"E7"),subQ1]}),-1.0]])],"derivedFrom":subQ1})])]});var subQ8=makeQuery(id+"F1.opExtrude","SWEPT_FACE",FACE,{"disambiguationData":[OSD([subQ2])]});Q7=makeQuery(id+"F4.opChamfer","BLEND_EDGE",EDGE,{"blendedFrom":[makeQuery(id+"F3.boolean.opBoolean","SPLIT",EDGE,{"disambiguationData":[TD([subQ5])],"derivedFrom":subQ4}),makeQuery(id+"F3.boolean.opBoolean","SPLIT",FACE,{"disambiguationData":[TD([subQ5])],"derivedFrom":subQ8})],"blendedInto":[makeQuery(id+"F3.boolean.opBoolean","SPLIT",FACE,{"disambiguationData":[TD([subQ5])],"derivedFrom":subQ8})]});}
            var Q8;
            {var subQ0=sQuery(id+"F0.wireOp",EDGE,"E0.top");var subQ1=makeQuery(id+"F1.opExtrude","SWEPT_FACE",FACE,{"disambiguationData":[OSD([subQ0])]});var subQ2=sQuery(id+"F0.wireOp",EDGE,"E0.right");var subQ3=sQuery(id+"F2.wireOp",EDGE,"E13.trimOffspring");var subQ4=makeQuery(id+"F1.opExtrude","SWEPT_EDGE",EDGE,{"disambiguationData":[OSD([subQ0,subQ2])]});Q8=makeQuery(id+"F4.opChamfer","BLEND_EDGE",EDGE,{"blendedFrom":[makeQuery(id+"F3.boolean.opBoolean","SPLIT",EDGE,{"disambiguationData":[TD([makeQuery(id+"F3.opExtrude","SWEPT_FACE",FACE,{"disambiguationData":[OSD([subQ3]),TDD([makeQuery(id+"F2.imprint","IMPRINT",EDGE,{"disambiguationData":[TD([[makeQuery(id+"F2.imprint","INTERSECT",VERTEX,{"derivedFrom":[sQuery(id+"F2.wireOp",EDGE,"E7"),subQ3]}),-1.0]])],"derivedFrom":subQ3})])]})])],"derivedFrom":subQ4}),subQ1],"blendedInto":[subQ1]});}
            var Q9;
            {var subQ0=sQuery(id+"F0.wireOp",EDGE,"E0.top");var subQ1=makeQuery(id+"F1.opExtrude","SWEPT_FACE",FACE,{"disambiguationData":[OSD([subQ0])]});var subQ2=sQuery(id+"F0.wireOp",EDGE,"E0.right");var subQ3=sQuery(id+"F2.wireOp",EDGE,"E1");var subQ4=makeQuery(id+"F1.opExtrude","SWEPT_EDGE",EDGE,{"disambiguationData":[OSD([subQ0,subQ2])]});Q9=makeQuery(id+"F4.opChamfer","BLEND_EDGE",EDGE,{"blendedFrom":[makeQuery(id+"F3.boolean.opBoolean","SPLIT",EDGE,{"disambiguationData":[TD([makeQuery(id+"F3.opExtrude","SWEPT_FACE",FACE,{"disambiguationData":[OSD([subQ3]),TDD([makeQuery(id+"F2.imprint","IMPRINT",EDGE,{"disambiguationData":[TD([[makeQuery(id+"F2.imprint","INTERSECT",VERTEX,{"derivedFrom":[subQ3,sQuery(id+"F2.wireOp",EDGE,"E7")]}),-1.0]])],"derivedFrom":subQ3})])]})])],"derivedFrom":subQ4}),subQ1],"blendedInto":[subQ1]});}
            var Q10;
            {var subQ0=sQuery(id+"F0.wireOp",EDGE,"E0.top");var subQ1=makeQuery(id+"F1.opExtrude","SWEPT_FACE",FACE,{"disambiguationData":[OSD([subQ0])]});var subQ2=sQuery(id+"F0.wireOp",EDGE,"E0.left");var subQ3=sQuery(id+"F2.wireOp",EDGE,"E1");var subQ4=makeQuery(id+"F1.opExtrude","SWEPT_EDGE",EDGE,{"disambiguationData":[OSD([subQ0,subQ2])]});Q10=makeQuery(id+"F4.opChamfer","BLEND_EDGE",EDGE,{"blendedFrom":[makeQuery(id+"F3.boolean.opBoolean","SPLIT",EDGE,{"disambiguationData":[TD([makeQuery(id+"F3.opExtrude","SWEPT_FACE",FACE,{"disambiguationData":[OSD([subQ3]),TDD([makeQuery(id+"F2.imprint","IMPRINT",EDGE,{"disambiguationData":[TD([[makeQuery(id+"F2.imprint","INTERSECT",VERTEX,{"derivedFrom":[subQ3,sQuery(id+"F2.wireOp",EDGE,"E3")]}),1.0]])],"derivedFrom":subQ3})])]})])],"derivedFrom":subQ4}),subQ1],"blendedInto":[subQ1]});}
            var Q11;
            {var subQ0=sQuery(id+"F0.wireOp",EDGE,"E0.top");var subQ1=makeQuery(id+"F1.opExtrude","SWEPT_FACE",FACE,{"disambiguationData":[OSD([subQ0])]});var subQ2=sQuery(id+"F0.wireOp",EDGE,"E0.left");var subQ3=sQuery(id+"F2.wireOp",EDGE,"E2");var subQ4=makeQuery(id+"F1.opExtrude","SWEPT_EDGE",EDGE,{"disambiguationData":[OSD([subQ0,subQ2])]});Q11=makeQuery(id+"F4.opChamfer","BLEND_EDGE",EDGE,{"blendedFrom":[makeQuery(id+"F3.boolean.opBoolean","SPLIT",EDGE,{"disambiguationData":[TD([makeQuery(id+"F3.opExtrude","SWEPT_FACE",FACE,{"disambiguationData":[OSD([subQ3]),TDD([makeQuery(id+"F2.imprint","IMPRINT",EDGE,{"disambiguationData":[TD([[makeQuery(id+"F2.imprint","INTERSECT",VERTEX,{"derivedFrom":[subQ3,sQuery(id+"F2.wireOp",EDGE,"E3")]}),1.0]])],"derivedFrom":subQ3})])]})])],"derivedFrom":subQ4}),subQ1],"blendedInto":[subQ1]});}
            fillet(context, id + "F19", {"entities" : qUnion([Q0, Q1, Q2, Q3, Q4, Q5, Q6, Q7, Q8, Q9, Q10, Q11]), "radius" : 1.27 * mm, "tangentPropagation" : true, "allowEdgeOverflow" : false});
        }
        {
            var Q0;
            Q0=makeQuery(id+"F3.boolean.opBoolean","COPY",EDGE,{"derivedFrom":makeQuery(id+"F3.opExtrude","SWEPT_EDGE",EDGE,{"disambiguationData":[OSD([sQuery(id+"F2.wireOp",EDGE,"E10"),sQuery(id+"F2.wireOp",EDGE,"E14.trimOffspring")])]})});
            var Q1;
            Q1=makeQuery(id+"F3.boolean.opBoolean","COPY",EDGE,{"derivedFrom":makeQuery(id+"F3.opExtrude","SWEPT_EDGE",EDGE,{"disambiguationData":[OSD([sQuery(id+"F2.wireOp",EDGE,"E9"),sQuery(id+"F2.wireOp",EDGE,"E13.trimOffspring")])]})});
            var Q2;
            Q2=makeQuery(id+"F3.boolean.opBoolean","COPY",EDGE,{"derivedFrom":makeQuery(id+"F3.opExtrude","SWEPT_EDGE",EDGE,{"disambiguationData":[OSD([sQuery(id+"F2.wireOp",EDGE,"E2"),sQuery(id+"F2.wireOp",EDGE,"E11")])]})});
            var Q3;
            Q3=makeQuery(id+"F3.boolean.opBoolean","COPY",EDGE,{"derivedFrom":makeQuery(id+"F3.opExtrude","SWEPT_EDGE",EDGE,{"disambiguationData":[OSD([sQuery(id+"F2.wireOp",EDGE,"E12"),sQuery(id+"F2.wireOp",EDGE,"E14.trimOffspring")])]})});
            fillet(context, id + "F20", {"entities" : qUnion([Q0, Q1, Q2, Q3]), "radius" : 0.38 * mm, "tangentPropagation" : true, "allowEdgeOverflow" : false});
        }
        {
            var Q0;
            {var subQ0=sQuery(id+"F17.wireOp",EDGE,"E133");var subQ1=sQuery(id+"F17.wireOp",EDGE,"E132.top");var subQ2=sQuery(id+"F17.wireOp",EDGE,"E132.left");var subQ3=sQuery(id+"F17.wireOp",EDGE,"E132.bottom");var subQ4=sQuery(id+"F17.wireOp",EDGE,"E126");var subQ5=sQuery(id+"F17.wireOp",EDGE,"E125.left");var subQ6=sQuery(id+"F17.wireOp",EDGE,"E125.top");var subQ7=sQuery(id+"F17.wireOp",EDGE,"E125.bottom");Q0=makeQuery(id+"F18.boolean.opBoolean","MERGE",FACE,{"derivedFrom":[makeQuery(id+"F1.opExtrude","SWEPT_FACE",FACE,{"disambiguationData":[OSD([sQuery(id+"F0.wireOp",EDGE,"E0.bottom")])]}),makeQuery(id+"F18.opExtrude","CAP_FACE",FACE,{"disambiguationData":[OSD([sQuery(id+"F17.wireOp",EDGE,"E103.bottom"),sQuery(id+"F17.wireOp",EDGE,"E103.top"),sQuery(id+"F17.wireOp",EDGE,"E103.left"),sQuery(id+"F17.wireOp",EDGE,"E103.right"),sQuery(id+"F17.wireOp",EDGE,"E105"),sQuery(id+"F17.wireOp",EDGE,"E108.trimOffspring"),sQuery(id+"F17.wireOp",EDGE,"E109.trimOffspring"),sQuery(id+"F17.wireOp",EDGE,"E110.trimOffspring")])],"isStart":true}),makeQuery(id+"F18.opExtrude","CAP_FACE",FACE,{"disambiguationData":[OSD([sQuery(id+"F17.wireOp",EDGE,"E111.bottom"),sQuery(id+"F17.wireOp",EDGE,"E111.top"),sQuery(id+"F17.wireOp",EDGE,"E111.left"),sQuery(id+"F17.wireOp",EDGE,"E111.right"),sQuery(id+"F17.wireOp",EDGE,"E113"),sQuery(id+"F17.wireOp",EDGE,"E114"),sQuery(id+"F17.wireOp",EDGE,"E115"),sQuery(id+"F17.wireOp",EDGE,"E116.trimOffspring")])],"isStart":true}),makeQuery(id+"F18.opExtrude","CAP_FACE",FACE,{"disambiguationData":[OSD([sQuery(id+"F17.wireOp",EDGE,"E118.bottom"),sQuery(id+"F17.wireOp",EDGE,"E118.top"),sQuery(id+"F17.wireOp",EDGE,"E118.left"),sQuery(id+"F17.wireOp",EDGE,"E118.right"),sQuery(id+"F17.wireOp",EDGE,"E120"),sQuery(id+"F17.wireOp",EDGE,"E121.trimOffspring"),sQuery(id+"F17.wireOp",EDGE,"E123.trimOffspring"),sQuery(id+"F17.wireOp",EDGE,"E124.trimOffspring")])],"isStart":true}),makeQuery(id+"F18.opExtrude","CAP_FACE",FACE,{"disambiguationData":[OSD([subQ7,sQuery(id+"F17.wireOp",EDGE,"E125.right"),subQ4,sQuery(id+"F17.wireOp",EDGE,"E127")])],"isStart":true}),makeQuery(id+"F18.opExtrude","CAP_FACE",FACE,{"disambiguationData":[OSD([subQ7,subQ5,subQ4])],"isStart":true}),makeQuery(id+"F18.opExtrude","CAP_FACE",FACE,{"disambiguationData":[OSD([subQ6,subQ4,sQuery(id+"F17.wireOp",EDGE,"E128"),sQuery(id+"F17.wireOp",EDGE,"E129.trimOffspring")])],"isStart":true}),makeQuery(id+"F18.opExtrude","CAP_FACE",FACE,{"disambiguationData":[OSD([subQ6,subQ5,subQ4])],"isStart":true}),makeQuery(id+"F18.opExtrude","CAP_FACE",FACE,{"disambiguationData":[OSD([subQ3,subQ2,subQ0])],"isStart":true}),makeQuery(id+"F18.opExtrude","CAP_FACE",FACE,{"disambiguationData":[OSD([subQ3,sQuery(id+"F17.wireOp",EDGE,"E132.right"),subQ0,sQuery(id+"F17.wireOp",EDGE,"E135.trimOffspring")])],"isStart":true}),makeQuery(id+"F18.opExtrude","CAP_FACE",FACE,{"disambiguationData":[OSD([subQ1,subQ2,subQ0])],"isStart":true}),makeQuery(id+"F18.opExtrude","CAP_FACE",FACE,{"disambiguationData":[OSD([subQ1,subQ0,sQuery(id+"F17.wireOp",EDGE,"E134.trimOffspring"),sQuery(id+"F17.wireOp",EDGE,"E138.trimOffspring")])],"isStart":true}),makeQuery(id+"F18.opExtrude","CAP_FACE",FACE,{"disambiguationData":[OSD([sQuery(id+"F17.wireOp",EDGE,"E139.bottom"),sQuery(id+"F17.wireOp",EDGE,"E139.top"),sQuery(id+"F17.wireOp",EDGE,"E139.left"),sQuery(id+"F17.wireOp",EDGE,"E139.right"),sQuery(id+"F17.wireOp",EDGE,"E140.trimOffspring"),sQuery(id+"F17.wireOp",EDGE,"E144"),sQuery(id+"F17.wireOp",EDGE,"E145"),sQuery(id+"F17.wireOp",EDGE,"E146")])],"isStart":true})]});}
            var sketch = newSketch(context, id + "F21", { "sketchPlane" : qUnion([Q0])});
            skLineSegment(sketch, "E147", {"start": v(56.62, 3.43) * mm, "end": v(58.4, 3.43) * mm});
            skLineSegment(sketch, "E148", {"start": v(58.4, 3.43) * mm, "end": v(58.4, 3.7) * mm});
            skLineSegment(sketch, "E149", {"start": v(58.4, 3.7) * mm, "end": v(56.62, 3.7) * mm});
            skLineSegment(sketch, "E150", {"start": v(56.62, 3.43) * mm, "end": v(56.87, 3.68) * mm});
            skLineSegment(sketch, "E151", {"start": v(56.87, 3.68) * mm, "end": v(57.12, 3.43) * mm});
            skLineSegment(sketch, "E152", {"start": v(57.12, 3.43) * mm, "end": v(57.38, 3.68) * mm});
            skLineSegment(sketch, "E153", {"start": v(57.38, 3.68) * mm, "end": v(57.63, 3.43) * mm});
            skLineSegment(sketch, "E154", {"start": v(57.63, 3.43) * mm, "end": v(57.89, 3.68) * mm});
            skLineSegment(sketch, "E155", {"start": v(57.89, 3.68) * mm, "end": v(58.14, 3.43) * mm});
            skLineSegment(sketch, "E156", {"start": v(58.14, 3.43) * mm, "end": v(58.4, 3.68) * mm});
            skLineSegment(sketch, "E157.MirrorCS", {"start": v(57.89, 2.67) * mm, "end": v(58.14, 2.92) * mm});
            skLineSegment(sketch, "E158.MirrorCS", {"start": v(58.4, 2.64) * mm, "end": v(56.62, 2.64) * mm});
            skLineSegment(sketch, "E159.MirrorCS", {"start": v(57.38, 2.67) * mm, "end": v(57.63, 2.92) * mm});
            skLineSegment(sketch, "E160.MirrorCS", {"start": v(58.14, 2.92) * mm, "end": v(58.4, 2.67) * mm});
            skLineSegment(sketch, "E161.MirrorCS", {"start": v(57.12, 2.92) * mm, "end": v(57.38, 2.67) * mm});
            skLineSegment(sketch, "E162.MirrorCS", {"start": v(56.87, 2.67) * mm, "end": v(57.12, 2.92) * mm});
            skLineSegment(sketch, "E163.MirrorCS", {"start": v(56.62, 2.92) * mm, "end": v(58.4, 2.92) * mm});
            skLineSegment(sketch, "E164.MirrorCS", {"start": v(58.4, 2.92) * mm, "end": v(58.4, 2.64) * mm});
            skLineSegment(sketch, "E165.MirrorCS", {"start": v(56.62, 2.92) * mm, "end": v(56.87, 2.67) * mm});
            skLineSegment(sketch, "E166.MirrorCS", {"start": v(57.63, 2.92) * mm, "end": v(57.89, 2.67) * mm});
            skSolve(sketch);
        }
        {
            var Q0;
            {var subQ0=sQuery(id+"F21.wireOp",EDGE,"E149");Q0=makeQuery(id+"F21.imprint","IMPRINT",FACE,{"disambiguationData":[TD([[makeQuery(id+"F21.imprint","IMPRINT",EDGE,{"derivedFrom":subQ0}),1.0]])]});}
            var Q1;
            Q1=makeQuery(id+"F21.imprint","IMPRINT",FACE,{"disambiguationData":[TD([[makeQuery(id+"F21.imprint","IMPRINT",EDGE,{"derivedFrom":sQuery(id+"F21.wireOp",EDGE,"E157.MirrorCS")}),-1.0]])]});
            extrude(context, id + "F22", {"entities" : qUnion([Q0, Q1]), "operationType" : NewBodyOperationType.ADD, "oppositeDirection" : true, "depth" : 12.7 * mm, "offsetDistance" : 25.4 * mm});
        }
        {
            var Q0;
            Q0=makeQuery(id+"F22.boolean.opBoolean","MERGE",FACE,{"derivedFrom":[makeQuery(id+"F18.opExtrude","SWEPT_FACE",FACE,{"disambiguationData":[OSD([sQuery(id+"F17.wireOp",EDGE,"E103.bottom")])]}),makeQuery(id+"F22.opExtrude","SWEPT_FACE",FACE,{"disambiguationData":[OSD([sQuery(id+"F21.wireOp",EDGE,"E149")])]})]});
            var sketch = newSketch(context, id + "F23", { "sketchPlane" : qUnion([Q0])});
            skLineSegment(sketch, "E167", {"start": v(55.55, 0) * mm, "end": v(58.4, 2.84) * mm});
            skLineSegment(sketch, "E168", {"start": v(58.4, 2.84) * mm, "end": v(58.4, 0) * mm});
            skLineSegment(sketch, "E169", {"start": v(58.4, 0) * mm, "end": v(55.55, 0) * mm});
            skSolve(sketch);
        }
        {
            var Q0;
            Q0=makeQuery(id+"F23.imprint","IMPRINT",FACE,{"disambiguationData":[TD([[makeQuery(id+"F23.imprint","IMPRINT",EDGE,{"derivedFrom":sQuery(id+"F23.wireOp",EDGE,"E167")}),1.0]])]});
            extrude(context, id + "F24", {"entities" : qUnion([Q0]), "operationType" : NewBodyOperationType.REMOVE, "oppositeDirection" : true, "depth" : 25.4 * mm, "offsetDistance" : 25.4 * mm});
        }
        {
            var Q0;
            {var subQ0=sQuery(id+"F17.wireOp",EDGE,"E108.trimOffspring");var subQ1=sQuery(id+"F17.wireOp",EDGE,"E103.right");var subQ2=sQuery(id+"F17.wireOp",EDGE,"E133");var subQ3=sQuery(id+"F17.wireOp",EDGE,"E132.top");var subQ4=sQuery(id+"F17.wireOp",EDGE,"E132.left");var subQ5=sQuery(id+"F17.wireOp",EDGE,"E132.bottom");var subQ6=sQuery(id+"F17.wireOp",EDGE,"E126");var subQ7=sQuery(id+"F17.wireOp",EDGE,"E125.left");var subQ8=sQuery(id+"F17.wireOp",EDGE,"E125.top");var subQ9=sQuery(id+"F17.wireOp",EDGE,"E125.bottom");Q0=makeQuery(id+"F22.boolean.opBoolean","MERGE",FACE,{"derivedFrom":[makeQuery(id+"F18.boolean.opBoolean","MERGE",FACE,{"derivedFrom":[makeQuery(id+"F1.opExtrude","SWEPT_FACE",FACE,{"disambiguationData":[OSD([sQuery(id+"F0.wireOp",EDGE,"E0.bottom")])]}),makeQuery(id+"F18.opExtrude","CAP_FACE",FACE,{"disambiguationData":[OSD([sQuery(id+"F17.wireOp",EDGE,"E103.bottom"),sQuery(id+"F17.wireOp",EDGE,"E103.top"),sQuery(id+"F17.wireOp",EDGE,"E103.left"),subQ1,sQuery(id+"F17.wireOp",EDGE,"E105"),subQ0,sQuery(id+"F17.wireOp",EDGE,"E109.trimOffspring"),sQuery(id+"F17.wireOp",EDGE,"E110.trimOffspring")])],"isStart":true}),makeQuery(id+"F18.opExtrude","CAP_FACE",FACE,{"disambiguationData":[OSD([sQuery(id+"F17.wireOp",EDGE,"E111.bottom"),sQuery(id+"F17.wireOp",EDGE,"E111.top"),sQuery(id+"F17.wireOp",EDGE,"E111.left"),sQuery(id+"F17.wireOp",EDGE,"E111.right"),sQuery(id+"F17.wireOp",EDGE,"E113"),sQuery(id+"F17.wireOp",EDGE,"E114"),sQuery(id+"F17.wireOp",EDGE,"E115"),sQuery(id+"F17.wireOp",EDGE,"E116.trimOffspring")])],"isStart":true}),makeQuery(id+"F18.opExtrude","CAP_FACE",FACE,{"disambiguationData":[OSD([sQuery(id+"F17.wireOp",EDGE,"E118.bottom"),sQuery(id+"F17.wireOp",EDGE,"E118.top"),sQuery(id+"F17.wireOp",EDGE,"E118.left"),sQuery(id+"F17.wireOp",EDGE,"E118.right"),sQuery(id+"F17.wireOp",EDGE,"E120"),sQuery(id+"F17.wireOp",EDGE,"E121.trimOffspring"),sQuery(id+"F17.wireOp",EDGE,"E123.trimOffspring"),sQuery(id+"F17.wireOp",EDGE,"E124.trimOffspring")])],"isStart":true}),makeQuery(id+"F18.opExtrude","CAP_FACE",FACE,{"disambiguationData":[OSD([subQ9,sQuery(id+"F17.wireOp",EDGE,"E125.right"),subQ6,sQuery(id+"F17.wireOp",EDGE,"E127")])],"isStart":true}),makeQuery(id+"F18.opExtrude","CAP_FACE",FACE,{"disambiguationData":[OSD([subQ9,subQ7,subQ6])],"isStart":true}),makeQuery(id+"F18.opExtrude","CAP_FACE",FACE,{"disambiguationData":[OSD([subQ8,subQ6,sQuery(id+"F17.wireOp",EDGE,"E128"),sQuery(id+"F17.wireOp",EDGE,"E129.trimOffspring")])],"isStart":true}),makeQuery(id+"F18.opExtrude","CAP_FACE",FACE,{"disambiguationData":[OSD([subQ8,subQ7,subQ6])],"isStart":true}),makeQuery(id+"F18.opExtrude","CAP_FACE",FACE,{"disambiguationData":[OSD([subQ5,subQ4,subQ2])],"isStart":true}),makeQuery(id+"F18.opExtrude","CAP_FACE",FACE,{"disambiguationData":[OSD([subQ5,sQuery(id+"F17.wireOp",EDGE,"E132.right"),subQ2,sQuery(id+"F17.wireOp",EDGE,"E135.trimOffspring")])],"isStart":true}),makeQuery(id+"F18.opExtrude","CAP_FACE",FACE,{"disambiguationData":[OSD([subQ3,subQ4,subQ2])],"isStart":true}),makeQuery(id+"F18.opExtrude","CAP_FACE",FACE,{"disambiguationData":[OSD([subQ3,subQ2,sQuery(id+"F17.wireOp",EDGE,"E134.trimOffspring"),sQuery(id+"F17.wireOp",EDGE,"E138.trimOffspring")])],"isStart":true}),makeQuery(id+"F18.opExtrude","CAP_FACE",FACE,{"disambiguationData":[OSD([sQuery(id+"F17.wireOp",EDGE,"E139.bottom"),sQuery(id+"F17.wireOp",EDGE,"E139.top"),sQuery(id+"F17.wireOp",EDGE,"E139.left"),sQuery(id+"F17.wireOp",EDGE,"E139.right"),sQuery(id+"F17.wireOp",EDGE,"E140.trimOffspring"),sQuery(id+"F17.wireOp",EDGE,"E144"),sQuery(id+"F17.wireOp",EDGE,"E145"),sQuery(id+"F17.wireOp",EDGE,"E146")])],"isStart":true})]}),makeQuery(id+"F22.opExtrude","CAP_FACE",FACE,{"disambiguationData":[OSD([subQ1,sQuery(id+"F21.wireOp",EDGE,"E148"),sQuery(id+"F21.wireOp",EDGE,"E149"),sQuery(id+"F21.wireOp",EDGE,"E150"),sQuery(id+"F21.wireOp",EDGE,"E151"),sQuery(id+"F21.wireOp",EDGE,"E152"),sQuery(id+"F21.wireOp",EDGE,"E153"),sQuery(id+"F21.wireOp",EDGE,"E154"),sQuery(id+"F21.wireOp",EDGE,"E155"),sQuery(id+"F21.wireOp",EDGE,"E156")])],"isStart":true}),makeQuery(id+"F22.opExtrude","CAP_FACE",FACE,{"disambiguationData":[OSD([subQ0,sQuery(id+"F21.wireOp",EDGE,"E157.MirrorCS"),sQuery(id+"F21.wireOp",EDGE,"E158.MirrorCS"),sQuery(id+"F21.wireOp",EDGE,"E159.MirrorCS"),sQuery(id+"F21.wireOp",EDGE,"E160.MirrorCS"),sQuery(id+"F21.wireOp",EDGE,"E161.MirrorCS"),sQuery(id+"F21.wireOp",EDGE,"E162.MirrorCS"),sQuery(id+"F21.wireOp",EDGE,"E164.MirrorCS"),sQuery(id+"F21.wireOp",EDGE,"E165.MirrorCS"),sQuery(id+"F21.wireOp",EDGE,"E166.MirrorCS")])],"isStart":true})]});}
            var sketch = newSketch(context, id + "F25", { "sketchPlane" : qUnion([Q0])});
            skLineSegment(sketch, "E170", {"start": v(35.93, 3.43) * mm, "end": v(37.7, 3.43) * mm});
            skLineSegment(sketch, "E171", {"start": v(37.7, 3.43) * mm, "end": v(37.7, 3.7) * mm});
            skLineSegment(sketch, "E172", {"start": v(37.7, 3.7) * mm, "end": v(35.93, 3.7) * mm});
            skLineSegment(sketch, "E173", {"start": v(35.93, 3.43) * mm, "end": v(36.18, 3.68) * mm});
            skLineSegment(sketch, "E174", {"start": v(36.18, 3.68) * mm, "end": v(36.44, 3.43) * mm});
            skLineSegment(sketch, "E175", {"start": v(36.44, 3.43) * mm, "end": v(36.7, 3.68) * mm});
            skLineSegment(sketch, "E176", {"start": v(36.7, 3.68) * mm, "end": v(36.94, 3.43) * mm});
            skLineSegment(sketch, "E177", {"start": v(36.94, 3.43) * mm, "end": v(37.2, 3.68) * mm});
            skLineSegment(sketch, "E178", {"start": v(37.2, 3.68) * mm, "end": v(37.45, 3.43) * mm});
            skLineSegment(sketch, "E179", {"start": v(37.45, 3.43) * mm, "end": v(37.7, 3.68) * mm});
            skLineSegment(sketch, "E180.MirrorCS", {"start": v(37.2, 2.67) * mm, "end": v(37.45, 2.92) * mm});
            skLineSegment(sketch, "E181.MirrorCS", {"start": v(37.7, 2.64) * mm, "end": v(35.93, 2.64) * mm});
            skLineSegment(sketch, "E182.MirrorCS", {"start": v(36.7, 2.67) * mm, "end": v(36.94, 2.92) * mm});
            skLineSegment(sketch, "E183.MirrorCS", {"start": v(37.45, 2.92) * mm, "end": v(37.7, 2.67) * mm});
            skLineSegment(sketch, "E184.MirrorCS", {"start": v(36.44, 2.92) * mm, "end": v(36.7, 2.67) * mm});
            skLineSegment(sketch, "E185.MirrorCS", {"start": v(36.18, 2.67) * mm, "end": v(36.44, 2.92) * mm});
            skLineSegment(sketch, "E186.MirrorCS", {"start": v(35.93, 2.92) * mm, "end": v(37.7, 2.92) * mm});
            skLineSegment(sketch, "E187.MirrorCS", {"start": v(37.7, 2.92) * mm, "end": v(37.7, 2.64) * mm});
            skLineSegment(sketch, "E188.MirrorCS", {"start": v(35.93, 2.92) * mm, "end": v(36.18, 2.67) * mm});
            skLineSegment(sketch, "E189.MirrorCS", {"start": v(36.94, 2.92) * mm, "end": v(37.2, 2.67) * mm});
            skLineSegment(sketch, "E190.MirrorCS", {"start": v(43.3, 2.92) * mm, "end": v(43.3, 2.64) * mm});
            skLineSegment(sketch, "E191.MirrorCS", {"start": v(43.82, 3.68) * mm, "end": v(43.56, 3.43) * mm});
            skLineSegment(sketch, "E192.MirrorCS", {"start": v(43.3, 3.43) * mm, "end": v(43.3, 3.7) * mm});
            skLineSegment(sketch, "E193.MirrorCS", {"start": v(43.3, 2.64) * mm, "end": v(45.09, 2.64) * mm});
            skLineSegment(sketch, "E194.MirrorCS", {"start": v(44.07, 3.43) * mm, "end": v(43.82, 3.68) * mm});
            skLineSegment(sketch, "E195.MirrorCS", {"start": v(44.83, 2.67) * mm, "end": v(44.58, 2.92) * mm});
            skLineSegment(sketch, "E196.MirrorCS", {"start": v(43.56, 2.92) * mm, "end": v(43.3, 2.67) * mm});
            skLineSegment(sketch, "E197.MirrorCS", {"start": v(44.58, 2.92) * mm, "end": v(44.32, 2.67) * mm});
            skLineSegment(sketch, "E198.MirrorCS", {"start": v(45.09, 2.92) * mm, "end": v(43.3, 2.92) * mm});
            skLineSegment(sketch, "E199.MirrorCS", {"start": v(44.07, 2.92) * mm, "end": v(43.82, 2.67) * mm});
            skLineSegment(sketch, "E200.MirrorCS", {"start": v(44.32, 2.67) * mm, "end": v(44.07, 2.92) * mm});
            skLineSegment(sketch, "E201.MirrorCS", {"start": v(45.09, 3.43) * mm, "end": v(43.3, 3.43) * mm});
            skLineSegment(sketch, "E202.MirrorCS", {"start": v(44.83, 3.68) * mm, "end": v(44.58, 3.43) * mm});
            skLineSegment(sketch, "E203.MirrorCS", {"start": v(45.09, 2.92) * mm, "end": v(44.83, 2.67) * mm});
            skLineSegment(sketch, "E204.MirrorCS", {"start": v(45.09, 3.43) * mm, "end": v(44.83, 3.68) * mm});
            skLineSegment(sketch, "E205.MirrorCS", {"start": v(44.58, 3.43) * mm, "end": v(44.32, 3.68) * mm});
            skLineSegment(sketch, "E206.MirrorCS", {"start": v(43.56, 3.43) * mm, "end": v(43.3, 3.68) * mm});
            skLineSegment(sketch, "E207.MirrorCS", {"start": v(44.32, 3.68) * mm, "end": v(44.07, 3.43) * mm});
            skLineSegment(sketch, "E208.MirrorCS", {"start": v(43.3, 3.7) * mm, "end": v(45.09, 3.7) * mm});
            skLineSegment(sketch, "E209.MirrorCS", {"start": v(43.82, 2.67) * mm, "end": v(43.56, 2.92) * mm});
            skLineSegment(sketch, "E210", {"start": v(15.24, 3.43) * mm, "end": v(17.02, 3.43) * mm});
            skLineSegment(sketch, "E211", {"start": v(17.02, 3.43) * mm, "end": v(17.02, 3.7) * mm});
            skLineSegment(sketch, "E212", {"start": v(17.02, 3.7) * mm, "end": v(15.24, 3.7) * mm});
            skLineSegment(sketch, "E213", {"start": v(15.24, 3.43) * mm, "end": v(15.5, 3.68) * mm});
            skLineSegment(sketch, "E214", {"start": v(15.5, 3.68) * mm, "end": v(15.75, 3.43) * mm});
            skLineSegment(sketch, "E215", {"start": v(15.75, 3.43) * mm, "end": v(16, 3.68) * mm});
            skLineSegment(sketch, "E216", {"start": v(16, 3.68) * mm, "end": v(16.26, 3.43) * mm});
            skLineSegment(sketch, "E217", {"start": v(16.26, 3.43) * mm, "end": v(16.51, 3.68) * mm});
            skLineSegment(sketch, "E218", {"start": v(16.5, 3.68) * mm, "end": v(16.76, 3.43) * mm});
            skLineSegment(sketch, "E219", {"start": v(16.76, 3.43) * mm, "end": v(17.02, 3.68) * mm});
            skLineSegment(sketch, "E220.MirrorCS", {"start": v(16.5, 2.67) * mm, "end": v(16.76, 2.92) * mm});
            skLineSegment(sketch, "E221.MirrorCS", {"start": v(17.02, 2.64) * mm, "end": v(15.24, 2.64) * mm});
            skLineSegment(sketch, "E222.MirrorCS", {"start": v(16, 2.67) * mm, "end": v(16.26, 2.92) * mm});
            skLineSegment(sketch, "E223.MirrorCS", {"start": v(16.76, 2.92) * mm, "end": v(17.02, 2.67) * mm});
            skLineSegment(sketch, "E224.MirrorCS", {"start": v(15.75, 2.92) * mm, "end": v(16, 2.67) * mm});
            skLineSegment(sketch, "E225.MirrorCS", {"start": v(15.5, 2.67) * mm, "end": v(15.75, 2.92) * mm});
            skLineSegment(sketch, "E226.MirrorCS", {"start": v(15.24, 2.92) * mm, "end": v(17.02, 2.92) * mm});
            skLineSegment(sketch, "E227.MirrorCS", {"start": v(17.02, 2.92) * mm, "end": v(17.02, 2.64) * mm});
            skLineSegment(sketch, "E228.MirrorCS", {"start": v(15.24, 2.92) * mm, "end": v(15.5, 2.67) * mm});
            skLineSegment(sketch, "E229.MirrorCS", {"start": v(16.26, 2.92) * mm, "end": v(16.5, 2.67) * mm});
            skLineSegment(sketch, "E230.MirrorCS", {"start": v(22.62, 2.92) * mm, "end": v(22.62, 2.64) * mm});
            skLineSegment(sketch, "E231.MirrorCS", {"start": v(23.13, 3.68) * mm, "end": v(22.87, 3.43) * mm});
            skLineSegment(sketch, "E232.MirrorCS", {"start": v(22.62, 3.43) * mm, "end": v(22.62, 3.7) * mm});
            skLineSegment(sketch, "E233.MirrorCS", {"start": v(22.62, 2.64) * mm, "end": v(24.4, 2.64) * mm});
            skLineSegment(sketch, "E234.MirrorCS", {"start": v(23.38, 3.43) * mm, "end": v(23.13, 3.68) * mm});
            skLineSegment(sketch, "E235.MirrorCS", {"start": v(24.14, 2.67) * mm, "end": v(23.89, 2.92) * mm});
            skLineSegment(sketch, "E236.MirrorCS", {"start": v(22.87, 2.92) * mm, "end": v(22.62, 2.67) * mm});
            skLineSegment(sketch, "E237.MirrorCS", {"start": v(23.89, 2.92) * mm, "end": v(23.63, 2.67) * mm});
            skLineSegment(sketch, "E238.MirrorCS", {"start": v(24.4, 2.92) * mm, "end": v(22.62, 2.92) * mm});
            skLineSegment(sketch, "E239.MirrorCS", {"start": v(23.38, 2.92) * mm, "end": v(23.13, 2.67) * mm});
            skLineSegment(sketch, "E240.MirrorCS", {"start": v(23.63, 2.67) * mm, "end": v(23.38, 2.92) * mm});
            skLineSegment(sketch, "E241.MirrorCS", {"start": v(24.4, 3.43) * mm, "end": v(22.62, 3.43) * mm});
            skLineSegment(sketch, "E242.MirrorCS", {"start": v(24.14, 3.68) * mm, "end": v(23.89, 3.43) * mm});
            skLineSegment(sketch, "E243.MirrorCS", {"start": v(24.4, 2.92) * mm, "end": v(24.14, 2.67) * mm});
            skLineSegment(sketch, "E244.MirrorCS", {"start": v(24.4, 3.43) * mm, "end": v(24.14, 3.68) * mm});
            skLineSegment(sketch, "E245.MirrorCS", {"start": v(23.89, 3.43) * mm, "end": v(23.63, 3.68) * mm});
            skLineSegment(sketch, "E246.MirrorCS", {"start": v(22.87, 3.43) * mm, "end": v(22.62, 3.68) * mm});
            skLineSegment(sketch, "E247.MirrorCS", {"start": v(23.63, 3.68) * mm, "end": v(23.38, 3.43) * mm});
            skLineSegment(sketch, "E248.MirrorCS", {"start": v(22.62, 3.7) * mm, "end": v(24.4, 3.7) * mm});
            skLineSegment(sketch, "E249.MirrorCS", {"start": v(23.13, 2.67) * mm, "end": v(22.87, 2.92) * mm});
            skSolve(sketch);
        }
        {
            var Q0;
            {var subQ0=sQuery(id+"F25.wireOp",EDGE,"E212");Q0=makeQuery(id+"F25.imprint","IMPRINT",FACE,{"disambiguationData":[TD([[makeQuery(id+"F25.imprint","IMPRINT",EDGE,{"derivedFrom":subQ0}),-1.0]])]});}
            var Q1;
            Q1=makeQuery(id+"F25.imprint","IMPRINT",FACE,{"disambiguationData":[TD([[makeQuery(id+"F25.imprint","IMPRINT",EDGE,{"derivedFrom":sQuery(id+"F25.wireOp",EDGE,"E220.MirrorCS")}),-1.0]])]});
            var Q2;
            {var subQ1=sQuery(id+"F25.wireOp",EDGE,"E233.MirrorCS");Q2=makeQuery(id+"F25.imprint","IMPRINT",FACE,{"disambiguationData":[TD([[makeQuery(id+"F25.imprint","IMPRINT",EDGE,{"derivedFrom":subQ1}),1.0]])]});}
            var Q3;
            Q3=makeQuery(id+"F25.imprint","IMPRINT",FACE,{"disambiguationData":[TD([[makeQuery(id+"F25.imprint","IMPRINT",EDGE,{"derivedFrom":sQuery(id+"F25.wireOp",EDGE,"E231.MirrorCS")}),-1.0]])]});
            var Q4;
            {var subQ0=sQuery(id+"F25.wireOp",EDGE,"E172");Q4=makeQuery(id+"F25.imprint","IMPRINT",FACE,{"disambiguationData":[TD([[makeQuery(id+"F25.imprint","IMPRINT",EDGE,{"derivedFrom":subQ0}),-1.0]])]});}
            var Q5;
            Q5=makeQuery(id+"F25.imprint","IMPRINT",FACE,{"disambiguationData":[TD([[makeQuery(id+"F25.imprint","IMPRINT",EDGE,{"derivedFrom":sQuery(id+"F25.wireOp",EDGE,"E180.MirrorCS")}),-1.0]])]});
            var Q6;
            Q6=makeQuery(id+"F25.imprint","IMPRINT",FACE,{"disambiguationData":[TD([[makeQuery(id+"F25.imprint","IMPRINT",EDGE,{"derivedFrom":sQuery(id+"F25.wireOp",EDGE,"E191.MirrorCS")}),-1.0]])]});
            var Q7;
            {var subQ1=sQuery(id+"F25.wireOp",EDGE,"E193.MirrorCS");Q7=makeQuery(id+"F25.imprint","IMPRINT",FACE,{"disambiguationData":[TD([[makeQuery(id+"F25.imprint","IMPRINT",EDGE,{"derivedFrom":subQ1}),1.0]])]});}
            extrude(context, id + "F26", {"entities" : qUnion([Q0, Q1, Q2, Q3, Q4, Q5, Q6, Q7]), "operationType" : NewBodyOperationType.ADD, "oppositeDirection" : true, "depth" : 12.7 * mm, "offsetDistance" : 25.4 * mm});
        }
        {
            var Q0;
            {var subQ0=sQuery(id+"F17.wireOp",EDGE,"E125.right");var subQ1=sQuery(id+"F17.wireOp",EDGE,"E129.trimOffspring");var subQ2=sQuery(id+"F17.wireOp",EDGE,"E134.trimOffspring");var subQ3=sQuery(id+"F17.wireOp",EDGE,"E132.right");var subQ4=sQuery(id+"F17.wireOp",EDGE,"E111.right");var subQ5=sQuery(id+"F17.wireOp",EDGE,"E116.trimOffspring");var subQ6=sQuery(id+"F17.wireOp",EDGE,"E124.trimOffspring");var subQ7=sQuery(id+"F17.wireOp",EDGE,"E118.right");var subQ8=sQuery(id+"F17.wireOp",EDGE,"E108.trimOffspring");var subQ9=sQuery(id+"F17.wireOp",EDGE,"E103.right");var subQ10=sQuery(id+"F17.wireOp",EDGE,"E133");var subQ11=sQuery(id+"F17.wireOp",EDGE,"E132.top");var subQ12=sQuery(id+"F17.wireOp",EDGE,"E132.left");var subQ13=sQuery(id+"F17.wireOp",EDGE,"E132.bottom");var subQ14=sQuery(id+"F17.wireOp",EDGE,"E126");var subQ15=sQuery(id+"F17.wireOp",EDGE,"E125.left");var subQ16=sQuery(id+"F17.wireOp",EDGE,"E125.top");var subQ17=sQuery(id+"F17.wireOp",EDGE,"E125.bottom");Q0=makeQuery(id+"F26.boolean.opBoolean","MERGE",FACE,{"derivedFrom":[makeQuery(id+"F22.boolean.opBoolean","MERGE",FACE,{"derivedFrom":[makeQuery(id+"F18.boolean.opBoolean","MERGE",FACE,{"derivedFrom":[makeQuery(id+"F1.opExtrude","SWEPT_FACE",FACE,{"disambiguationData":[OSD([sQuery(id+"F0.wireOp",EDGE,"E0.bottom")])]}),makeQuery(id+"F18.opExtrude","CAP_FACE",FACE,{"disambiguationData":[OSD([sQuery(id+"F17.wireOp",EDGE,"E103.bottom"),sQuery(id+"F17.wireOp",EDGE,"E103.top"),sQuery(id+"F17.wireOp",EDGE,"E103.left"),subQ9,sQuery(id+"F17.wireOp",EDGE,"E105"),subQ8,sQuery(id+"F17.wireOp",EDGE,"E109.trimOffspring"),sQuery(id+"F17.wireOp",EDGE,"E110.trimOffspring")])],"isStart":true}),makeQuery(id+"F18.opExtrude","CAP_FACE",FACE,{"disambiguationData":[OSD([sQuery(id+"F17.wireOp",EDGE,"E111.bottom"),sQuery(id+"F17.wireOp",EDGE,"E111.top"),sQuery(id+"F17.wireOp",EDGE,"E111.left"),subQ4,sQuery(id+"F17.wireOp",EDGE,"E113"),sQuery(id+"F17.wireOp",EDGE,"E114"),sQuery(id+"F17.wireOp",EDGE,"E115"),subQ5])],"isStart":true}),makeQuery(id+"F18.opExtrude","CAP_FACE",FACE,{"disambiguationData":[OSD([sQuery(id+"F17.wireOp",EDGE,"E118.bottom"),sQuery(id+"F17.wireOp",EDGE,"E118.top"),sQuery(id+"F17.wireOp",EDGE,"E118.left"),subQ7,sQuery(id+"F17.wireOp",EDGE,"E120"),sQuery(id+"F17.wireOp",EDGE,"E121.trimOffspring"),sQuery(id+"F17.wireOp",EDGE,"E123.trimOffspring"),subQ6])],"isStart":true}),makeQuery(id+"F18.opExtrude","CAP_FACE",FACE,{"disambiguationData":[OSD([subQ17,subQ0,subQ14,sQuery(id+"F17.wireOp",EDGE,"E127")])],"isStart":true}),makeQuery(id+"F18.opExtrude","CAP_FACE",FACE,{"disambiguationData":[OSD([subQ17,subQ15,subQ14])],"isStart":true}),makeQuery(id+"F18.opExtrude","CAP_FACE",FACE,{"disambiguationData":[OSD([subQ16,subQ14,sQuery(id+"F17.wireOp",EDGE,"E128"),subQ1])],"isStart":true}),makeQuery(id+"F18.opExtrude","CAP_FACE",FACE,{"disambiguationData":[OSD([subQ16,subQ15,subQ14])],"isStart":true}),makeQuery(id+"F18.opExtrude","CAP_FACE",FACE,{"disambiguationData":[OSD([subQ13,subQ12,subQ10])],"isStart":true}),makeQuery(id+"F18.opExtrude","CAP_FACE",FACE,{"disambiguationData":[OSD([subQ13,subQ3,subQ10,sQuery(id+"F17.wireOp",EDGE,"E135.trimOffspring")])],"isStart":true}),makeQuery(id+"F18.opExtrude","CAP_FACE",FACE,{"disambiguationData":[OSD([subQ11,subQ12,subQ10])],"isStart":true}),makeQuery(id+"F18.opExtrude","CAP_FACE",FACE,{"disambiguationData":[OSD([subQ11,subQ10,subQ2,sQuery(id+"F17.wireOp",EDGE,"E138.trimOffspring")])],"isStart":true}),makeQuery(id+"F18.opExtrude","CAP_FACE",FACE,{"disambiguationData":[OSD([sQuery(id+"F17.wireOp",EDGE,"E139.bottom"),sQuery(id+"F17.wireOp",EDGE,"E139.top"),sQuery(id+"F17.wireOp",EDGE,"E139.left"),sQuery(id+"F17.wireOp",EDGE,"E139.right"),sQuery(id+"F17.wireOp",EDGE,"E140.trimOffspring"),sQuery(id+"F17.wireOp",EDGE,"E144"),sQuery(id+"F17.wireOp",EDGE,"E145"),sQuery(id+"F17.wireOp",EDGE,"E146")])],"isStart":true})]}),makeQuery(id+"F22.opExtrude","CAP_FACE",FACE,{"disambiguationData":[OSD([subQ9,sQuery(id+"F21.wireOp",EDGE,"E148"),sQuery(id+"F21.wireOp",EDGE,"E149"),sQuery(id+"F21.wireOp",EDGE,"E150"),sQuery(id+"F21.wireOp",EDGE,"E151"),sQuery(id+"F21.wireOp",EDGE,"E152"),sQuery(id+"F21.wireOp",EDGE,"E153"),sQuery(id+"F21.wireOp",EDGE,"E154"),sQuery(id+"F21.wireOp",EDGE,"E155"),sQuery(id+"F21.wireOp",EDGE,"E156")])],"isStart":true}),makeQuery(id+"F22.opExtrude","CAP_FACE",FACE,{"disambiguationData":[OSD([subQ8,sQuery(id+"F21.wireOp",EDGE,"E157.MirrorCS"),sQuery(id+"F21.wireOp",EDGE,"E158.MirrorCS"),sQuery(id+"F21.wireOp",EDGE,"E159.MirrorCS"),sQuery(id+"F21.wireOp",EDGE,"E160.MirrorCS"),sQuery(id+"F21.wireOp",EDGE,"E161.MirrorCS"),sQuery(id+"F21.wireOp",EDGE,"E162.MirrorCS"),sQuery(id+"F21.wireOp",EDGE,"E164.MirrorCS"),sQuery(id+"F21.wireOp",EDGE,"E165.MirrorCS"),sQuery(id+"F21.wireOp",EDGE,"E166.MirrorCS")])],"isStart":true})]}),makeQuery(id+"F26.opExtrude","CAP_FACE",FACE,{"disambiguationData":[OSD([subQ7,sQuery(id+"F25.wireOp",EDGE,"E171"),sQuery(id+"F25.wireOp",EDGE,"E172"),sQuery(id+"F25.wireOp",EDGE,"E173"),sQuery(id+"F25.wireOp",EDGE,"E174"),sQuery(id+"F25.wireOp",EDGE,"E175"),sQuery(id+"F25.wireOp",EDGE,"E176"),sQuery(id+"F25.wireOp",EDGE,"E177"),sQuery(id+"F25.wireOp",EDGE,"E178"),sQuery(id+"F25.wireOp",EDGE,"E179")])],"isStart":true}),makeQuery(id+"F26.opExtrude","CAP_FACE",FACE,{"disambiguationData":[OSD([subQ6,sQuery(id+"F25.wireOp",EDGE,"E180.MirrorCS"),sQuery(id+"F25.wireOp",EDGE,"E181.MirrorCS"),sQuery(id+"F25.wireOp",EDGE,"E182.MirrorCS"),sQuery(id+"F25.wireOp",EDGE,"E183.MirrorCS"),sQuery(id+"F25.wireOp",EDGE,"E184.MirrorCS"),sQuery(id+"F25.wireOp",EDGE,"E185.MirrorCS"),sQuery(id+"F25.wireOp",EDGE,"E187.MirrorCS"),sQuery(id+"F25.wireOp",EDGE,"E188.MirrorCS"),sQuery(id+"F25.wireOp",EDGE,"E189.MirrorCS")])],"isStart":true}),makeQuery(id+"F26.opExtrude","CAP_FACE",FACE,{"disambiguationData":[OSD([subQ5,sQuery(id+"F25.wireOp",EDGE,"E190.MirrorCS"),sQuery(id+"F25.wireOp",EDGE,"E193.MirrorCS"),sQuery(id+"F25.wireOp",EDGE,"E195.MirrorCS"),sQuery(id+"F25.wireOp",EDGE,"E196.MirrorCS"),sQuery(id+"F25.wireOp",EDGE,"E197.MirrorCS"),sQuery(id+"F25.wireOp",EDGE,"E199.MirrorCS"),sQuery(id+"F25.wireOp",EDGE,"E200.MirrorCS"),sQuery(id+"F25.wireOp",EDGE,"E203.MirrorCS"),sQuery(id+"F25.wireOp",EDGE,"E209.MirrorCS")])],"isStart":true}),makeQuery(id+"F26.opExtrude","CAP_FACE",FACE,{"disambiguationData":[OSD([subQ4,sQuery(id+"F25.wireOp",EDGE,"E191.MirrorCS"),sQuery(id+"F25.wireOp",EDGE,"E192.MirrorCS"),sQuery(id+"F25.wireOp",EDGE,"E194.MirrorCS"),sQuery(id+"F25.wireOp",EDGE,"E202.MirrorCS"),sQuery(id+"F25.wireOp",EDGE,"E204.MirrorCS"),sQuery(id+"F25.wireOp",EDGE,"E205.MirrorCS"),sQuery(id+"F25.wireOp",EDGE,"E206.MirrorCS"),sQuery(id+"F25.wireOp",EDGE,"E207.MirrorCS"),sQuery(id+"F25.wireOp",EDGE,"E208.MirrorCS")])],"isStart":true}),makeQuery(id+"F26.opExtrude","CAP_FACE",FACE,{"disambiguationData":[OSD([subQ3,sQuery(id+"F25.wireOp",EDGE,"E211"),sQuery(id+"F25.wireOp",EDGE,"E212"),sQuery(id+"F25.wireOp",EDGE,"E213"),sQuery(id+"F25.wireOp",EDGE,"E214"),sQuery(id+"F25.wireOp",EDGE,"E215"),sQuery(id+"F25.wireOp",EDGE,"E216"),sQuery(id+"F25.wireOp",EDGE,"E217"),sQuery(id+"F25.wireOp",EDGE,"E218"),sQuery(id+"F25.wireOp",EDGE,"E219")])],"isStart":true}),makeQuery(id+"F26.opExtrude","CAP_FACE",FACE,{"disambiguationData":[OSD([subQ2,sQuery(id+"F25.wireOp",EDGE,"E220.MirrorCS"),sQuery(id+"F25.wireOp",EDGE,"E221.MirrorCS"),sQuery(id+"F25.wireOp",EDGE,"E222.MirrorCS"),sQuery(id+"F25.wireOp",EDGE,"E223.MirrorCS"),sQuery(id+"F25.wireOp",EDGE,"E224.MirrorCS"),sQuery(id+"F25.wireOp",EDGE,"E225.MirrorCS"),sQuery(id+"F25.wireOp",EDGE,"E227.MirrorCS"),sQuery(id+"F25.wireOp",EDGE,"E228.MirrorCS"),sQuery(id+"F25.wireOp",EDGE,"E229.MirrorCS")])],"isStart":true}),makeQuery(id+"F26.opExtrude","CAP_FACE",FACE,{"disambiguationData":[OSD([subQ1,sQuery(id+"F25.wireOp",EDGE,"E230.MirrorCS"),sQuery(id+"F25.wireOp",EDGE,"E233.MirrorCS"),sQuery(id+"F25.wireOp",EDGE,"E235.MirrorCS"),sQuery(id+"F25.wireOp",EDGE,"E236.MirrorCS"),sQuery(id+"F25.wireOp",EDGE,"E237.MirrorCS"),sQuery(id+"F25.wireOp",EDGE,"E239.MirrorCS"),sQuery(id+"F25.wireOp",EDGE,"E240.MirrorCS"),sQuery(id+"F25.wireOp",EDGE,"E243.MirrorCS"),sQuery(id+"F25.wireOp",EDGE,"E249.MirrorCS")])],"isStart":true}),makeQuery(id+"F26.opExtrude","CAP_FACE",FACE,{"disambiguationData":[OSD([subQ0,sQuery(id+"F25.wireOp",EDGE,"E231.MirrorCS"),sQuery(id+"F25.wireOp",EDGE,"E232.MirrorCS"),sQuery(id+"F25.wireOp",EDGE,"E234.MirrorCS"),sQuery(id+"F25.wireOp",EDGE,"E242.MirrorCS"),sQuery(id+"F25.wireOp",EDGE,"E244.MirrorCS"),sQuery(id+"F25.wireOp",EDGE,"E245.MirrorCS"),sQuery(id+"F25.wireOp",EDGE,"E246.MirrorCS"),sQuery(id+"F25.wireOp",EDGE,"E247.MirrorCS"),sQuery(id+"F25.wireOp",EDGE,"E248.MirrorCS")])],"isStart":true})]});}
            var sketch = newSketch(context, id + "F27", { "sketchPlane" : qUnion([Q0])});
            skLineSegment(sketch, "E250.MirrorCS", {"start": v(1.93, 2.92) * mm, "end": v(1.93, 2.64) * mm});
            skLineSegment(sketch, "E251.MirrorCS", {"start": v(2.44, 3.68) * mm, "end": v(2.18, 3.43) * mm});
            skLineSegment(sketch, "E252.MirrorCS", {"start": v(1.93, 3.43) * mm, "end": v(1.93, 3.7) * mm});
            skLineSegment(sketch, "E253.MirrorCS", {"start": v(1.93, 2.64) * mm, "end": v(3.7, 2.64) * mm});
            skLineSegment(sketch, "E254.MirrorCS", {"start": v(2.7, 3.43) * mm, "end": v(2.44, 3.68) * mm});
            skLineSegment(sketch, "E255.MirrorCS", {"start": v(3.45, 2.67) * mm, "end": v(3.2, 2.92) * mm});
            skLineSegment(sketch, "E256.MirrorCS", {"start": v(2.18, 2.92) * mm, "end": v(1.93, 2.67) * mm});
            skLineSegment(sketch, "E257.MirrorCS", {"start": v(3.2, 2.92) * mm, "end": v(2.95, 2.67) * mm});
            skLineSegment(sketch, "E258.MirrorCS", {"start": v(3.7, 2.92) * mm, "end": v(1.93, 2.92) * mm});
            skLineSegment(sketch, "E259.MirrorCS", {"start": v(2.7, 2.92) * mm, "end": v(2.44, 2.67) * mm});
            skLineSegment(sketch, "E260.MirrorCS", {"start": v(2.95, 2.67) * mm, "end": v(2.7, 2.92) * mm});
            skLineSegment(sketch, "E261.MirrorCS", {"start": v(3.7, 3.43) * mm, "end": v(1.93, 3.43) * mm});
            skLineSegment(sketch, "E262.MirrorCS", {"start": v(3.45, 3.68) * mm, "end": v(3.2, 3.43) * mm});
            skLineSegment(sketch, "E263.MirrorCS", {"start": v(3.7, 2.92) * mm, "end": v(3.45, 2.67) * mm});
            skLineSegment(sketch, "E264.MirrorCS", {"start": v(3.7, 3.43) * mm, "end": v(3.45, 3.68) * mm});
            skLineSegment(sketch, "E265.MirrorCS", {"start": v(3.2, 3.43) * mm, "end": v(2.95, 3.68) * mm});
            skLineSegment(sketch, "E266.MirrorCS", {"start": v(2.18, 3.43) * mm, "end": v(1.93, 3.68) * mm});
            skLineSegment(sketch, "E267.MirrorCS", {"start": v(2.95, 3.68) * mm, "end": v(2.7, 3.43) * mm});
            skLineSegment(sketch, "E268.MirrorCS", {"start": v(1.93, 3.7) * mm, "end": v(3.7, 3.7) * mm});
            skLineSegment(sketch, "E269.MirrorCS", {"start": v(2.44, 2.67) * mm, "end": v(2.18, 2.92) * mm});
            skSolve(sketch);
        }
        {
            var Q0;
            Q0=makeQuery(id+"F27.imprint","IMPRINT",FACE,{"disambiguationData":[TD([[makeQuery(id+"F27.imprint","IMPRINT",EDGE,{"derivedFrom":sQuery(id+"F27.wireOp",EDGE,"E251.MirrorCS")}),-1.0]])]});
            var Q1;
            {var subQ1=sQuery(id+"F27.wireOp",EDGE,"E253.MirrorCS");Q1=makeQuery(id+"F27.imprint","IMPRINT",FACE,{"disambiguationData":[TD([[makeQuery(id+"F27.imprint","IMPRINT",EDGE,{"derivedFrom":subQ1}),1.0]])]});}
            extrude(context, id + "F28", {"entities" : qUnion([Q0, Q1]), "operationType" : NewBodyOperationType.ADD, "oppositeDirection" : true, "depth" : 12.7 * mm, "offsetDistance" : 25.4 * mm});
        }
        {
            var Q0;
            Q0=makeQuery(id+"F28.boolean.opBoolean","MERGE",FACE,{"derivedFrom":[makeQuery(id+"F18.opExtrude","SWEPT_FACE",FACE,{"disambiguationData":[OSD([sQuery(id+"F17.wireOp",EDGE,"E139.bottom")])]}),makeQuery(id+"F28.opExtrude","SWEPT_FACE",FACE,{"disambiguationData":[OSD([sQuery(id+"F27.wireOp",EDGE,"E268.MirrorCS")])]})]});
            var sketch = newSketch(context, id + "F29", { "sketchPlane" : qUnion([Q0])});
            skLineSegment(sketch, "E270", {"start": v(1.93, 2.84) * mm, "end": v(4.78, 0) * mm});
            skLineSegment(sketch, "E271", {"start": v(4.78, 0) * mm, "end": v(1.93, 0) * mm});
            skLineSegment(sketch, "E272", {"start": v(1.93, 0) * mm, "end": v(1.93, 2.84) * mm});
            skSolve(sketch);
        }
        {
            var Q0;
            Q0=makeQuery(id+"F29.imprint","IMPRINT",FACE,{"disambiguationData":[TD([[makeQuery(id+"F29.imprint","IMPRINT",EDGE,{"derivedFrom":sQuery(id+"F29.wireOp",EDGE,"E270")}),1.0]])]});
            extrude(context, id + "F30", {"entities" : qUnion([Q0]), "operationType" : NewBodyOperationType.REMOVE, "oppositeDirection" : true, "depth" : 25.4 * mm, "offsetDistance" : 25.4 * mm});
        }
    });
